# Revit family: 859-002X-001 DN65-300
name_source: partatom
category: Pipe Accessories
units: mm (PartAtom-declared; Revit-internal decimal feet)

## family parameters
Always vertical = Yes
Cut with Voids When Loaded = No
Part Type = Valve - Breaks Into
Round Connector Dimension = Use Diameter
Shared = No
Work Plane-Based = No

## types (42) — shared parameters
10 = 10 mm  [stored 0.0328084 ft]
18 = 11 mm  [stored 0.0360892 ft]
3 = 3 mm  [stored 0.00984252 ft]
50 = 50 mm
8 = 8 mm  [stored 0.0262467 ft]
DN100_PN10/16 Flow range ( 14 - 34) = 859-0100-00-1140021
DN100_PN10/16 Flow range ( 23 - 57) = 859-0100-00-1140022
DN100_PN10/16 Flow range ( 47 - 113) = 859-0100-00-1140023
DN100_PN10/16 Flow range ( 7 - 18) = 859-0100-00-1140020
DN125_PN10/16 Flow range ( 13 - 32) = 859-0125-00-1140020
DN125_PN10/16 Flow range ( 21 - 52) = 859-0125-00-1140021
DN125_PN10/16 Flow range ( 32 - 80) = 859-0125-00-1140022
DN125_PN10/16 Flow range ( 48 - 118) = 859-0125-00-1140023
DN150_PN10/16 Flow range ( 115 - 254) = 859-0150-00-1140023
DN150_PN10/16 Flow range ( 30 - 75) = 859-0150-00-1140020
DN150_PN10/16 Flow range ( 50 - 150) = 859-0150-00-1140021
DN150_PN10/16 Flow range ( 80 - 200) = 859-0150-00-1140022
DN200_PN10 Flow range ( 115 - 290) = 859-0200-00-0140021
DN200_PN10 Flow range ( 150 - 339) = 859-0200-00-0140022
DN200_PN10 Flow range ( 190 - 339) = 859-0200-00-0140023
DN200_PN10 Flow range ( 50 - 130) = 859-0200-00-0140020
DN200_PN16 Flow range ( 115 - 290) = 859-0200-00-1140021
DN200_PN16 Flow range ( 150 - 365) = 859-0200-00-1140022
DN200_PN16 Flow range ( 190 - 452) = 859-0200-00-1140023
DN200_PN16 Flow range ( 50 - 130) = 859-0200-00-1140020
DN250_PN10 Flow range ( 140 - 350) = 859-0250-00-0140021
DN250_PN10 Flow range ( 230 - 530) = 859-0250-00-0140022
DN250_PN10 Flow range ( 280 - 530) = 859-0250-00-0140023
DN250_PN10 Flow range ( 85 - 200) = 859-0250-00-0140020
DN250_PN16 Flow range ( 140 - 350) = 859-0250-00-1140021
DN250_PN16 Flow range ( 230 - 570) = 859-0250-00-1140022
DN250_PN16 Flow range ( 280 - 690) = 859-0250-00-1140023
DN250_PN16 Flow range ( 85 - 200) = 859-0250-00-1140020
DN300_PN10 Flow range ( 120 - 300) = 859-0300-00-0140020
DN300_PN10 Flow range ( 175 - 430) = 859-0300-00-0140021
DN300_PN10 Flow range ( 340 - 762) = 859-0300-00-0140022
DN300_PN10 Flow range ( 460 - 762) = 859-0300-00-0140023
DN300_PN16 Flow range ( 120 - 300) = 859-0300-00-1140020
DN300_PN16 Flow range ( 175 - 430) = 859-0300-00-1140021
DN300_PN16 Flow range ( 340 - 825) = 859-0300-00-1140022
DN300_PN16 Flow range ( 460 - 1017) = 859-0300-00-1140023
DN65_PN10/16 Flow range ( 17 - 42) = 859-0065-00-1140022
DN65_PN10/16 Flow range ( 5 - 15) = 859-0065-00-1140020
DN65_PN10/16 Flow range ( 8 - 20) = 859-0065-00-1140021
DN80_PN10/16 Flow range ( 14 - 36) = 859-0080-00-1140021
DN80_PN10/16 Flow range ( 27 - 65) = 859-0080-00-1140022
DN80_PN10/16 Flow range ( 7 - 18) = 859-0080-00-1140020
Description_ = AVK CONTROL VALVE, CONSTANT FLOW, PN10/16
Orifice_FL_T = 14 mm  [stored 0.0459318 ft]
Search_table = 859-002X-001 DN65-300
URL_product_pages = https://www.avkvalves.com
zero-valued in all types: 0, Default Elevation

## per-type parameters (varying)
- DN065_PN10/16 Flow range ( 5 - 15): Actuator_L=72 mm; Actuator_L1=65 mm; Actuator_d=25 mm  [stored 0.082021 ft]; Body_H=111 mm; Body_Rib_L=46 mm; Bolt_Dia=20 mm  [stored 0.0656168 ft]; Bonnet_D=56 mm; Bonnet_D1=111 mm; Bonnet_R=117 mm; Bonnet_dim1=78 mm; Bonnet_dim1_H=30 mm  [stored 0.0984252 ft]; Bonnet_dim1_H1=188 mm; Bonnet_dim2=39 mm; Bonnet_dim3=29 mm  [stored 0.0951444 ft]; Bore=33 mm; Bore1=39 mm; Bore2=52 mm; Centre_D=25 mm  [stored 0.082021 ft]; Centre_D1=20 mm  [stored 0.0656168 ft]; Centre_nut=19 mm  [stored 0.062336 ft]; Control_dim1=7 mm  [stored 0.0229659 ft]; Control_dim2=35 mm  [stored 0.114829 ft]; Control_dim3=4 mm  [stored 0.0131234 ft]; Control_dim4=100 mm; Control_dim5=10 mm  [stored 0.0328084 ft]; Control_dim6=12 mm  [stored 0.0393701 ft]; Control_dim7=21 mm  [stored 0.0688976 ft]; D=93 mm; DN=65 mm; FL_T=19 mm  [stored 0.062336 ft]; H3=356 mm; H33=60 mm; H4=120 mm; L=290 mm; L3=128 mm; Nut_Dim1=25 mm  [stored 0.082021 ft]; Nut_Dim2=3 mm  [stored 0.00984252 ft]; Nut_T=15 mm  [stored 0.0492126 ft]; Orifice_FL=63 mm; Raised_R=24 mm  [stored 0.0787402 ft]; Raised_dis=3 mm  [stored 0.00984252 ft]; Sweep_R=11 mm  [stored 0.0360892 ft]; Thickness=11 mm  [stored 0.0360892 ft]; Thickness1=14 mm  [stored 0.0459318 ft]; Total_L=305 mm; W=124 mm; W1=131 mm; W11=104 mm; W2=161 mm; W22=129 mm; centre=51 mm; dim1=52 mm; nut_dim=56 mm; sweep=18 mm  [stored 0.0590551 ft]; sweep/2=4 mm  [stored 0.0131234 ft]; sweep1=8 mm  [stored 0.0262467 ft]; sweep_D=15 mm  [stored 0.0492126 ft]; sweep_H=171 mm; sweep_H1=42 mm  [stored 0.137795 ft]; sweep_box1=10 mm  [stored 0.0328084 ft]; sweep_box2=10 mm  [stored 0.0328084 ft]; w1=93 mm; w2=93 mm
- DN065_PN10/16 Flow range ( 8 - 20): Actuator_L=72 mm; Actuator_L1=65 mm; Actuator_d=25 mm  [stored 0.082021 ft]; Body_H=111 mm; Body_Rib_L=46 mm; Bolt_Dia=20 mm  [stored 0.0656168 ft]; Bonnet_D=56 mm; Bonnet_D1=111 mm; Bonnet_R=117 mm; Bonnet_dim1=78 mm; Bonnet_dim1_H=30 mm  [stored 0.0984252 ft]; Bonnet_dim1_H1=188 mm; Bonnet_dim2=39 mm; Bonnet_dim3=29 mm  [stored 0.0951444 ft]; Bore=33 mm; Bore1=39 mm; Bore2=52 mm; Centre_D=25 mm  [stored 0.082021 ft]; Centre_D1=20 mm  [stored 0.0656168 ft]; Centre_nut=19 mm  [stored 0.062336 ft]; Control_dim1=7 mm  [stored 0.0229659 ft]; Control_dim2=35 mm  [stored 0.114829 ft]; Control_dim3=4 mm  [stored 0.0131234 ft]; Control_dim4=100 mm; Control_dim5=10 mm  [stored 0.0328084 ft]; Control_dim6=12 mm  [stored 0.0393701 ft]; Control_dim7=21 mm  [stored 0.0688976 ft]; D=93 mm; DN=65 mm; FL_T=19 mm  [stored 0.062336 ft]; H3=356 mm; H33=60 mm; H4=120 mm; L=290 mm; L3=128 mm; Nut_Dim1=25 mm  [stored 0.082021 ft]; Nut_Dim2=3 mm  [stored 0.00984252 ft]; Nut_T=15 mm  [stored 0.0492126 ft]; Orifice_FL=63 mm; Raised_R=24 mm  [stored 0.0787402 ft]; Raised_dis=3 mm  [stored 0.00984252 ft]; Sweep_R=11 mm  [stored 0.0360892 ft]; Thickness=11 mm  [stored 0.0360892 ft]; Thickness1=14 mm  [stored 0.0459318 ft]; Total_L=305 mm; W=124 mm; W1=131 mm; W11=104 mm; W2=161 mm; W22=129 mm; centre=51 mm; dim1=52 mm; nut_dim=56 mm; sweep=18 mm  [stored 0.0590551 ft]; sweep/2=4 mm  [stored 0.0131234 ft]; sweep1=8 mm  [stored 0.0262467 ft]; sweep_D=15 mm  [stored 0.0492126 ft]; sweep_H=171 mm; sweep_H1=42 mm  [stored 0.137795 ft]; sweep_box1=10 mm  [stored 0.0328084 ft]; sweep_box2=10 mm  [stored 0.0328084 ft]; w1=93 mm; w2=93 mm
- DN065_PN10/16 Flow range ( 17 - 42): Actuator_L=72 mm; Actuator_L1=65 mm; Actuator_d=25 mm  [stored 0.082021 ft]; Body_H=111 mm; Body_Rib_L=46 mm; Bolt_Dia=20 mm  [stored 0.0656168 ft]; Bonnet_D=56 mm; Bonnet_D1=111 mm; Bonnet_R=117 mm; Bonnet_dim1=78 mm; Bonnet_dim1_H=30 mm  [stored 0.0984252 ft]; Bonnet_dim1_H1=188 mm; Bonnet_dim2=39 mm; Bonnet_dim3=29 mm  [stored 0.0951444 ft]; Bore=33 mm; Bore1=39 mm; Bore2=52 mm; Centre_D=25 mm  [stored 0.082021 ft]; Centre_D1=20 mm  [stored 0.0656168 ft]; Centre_nut=19 mm  [stored 0.062336 ft]; Control_dim1=7 mm  [stored 0.0229659 ft]; Control_dim2=35 mm  [stored 0.114829 ft]; Control_dim3=4 mm  [stored 0.0131234 ft]; Control_dim4=100 mm; Control_dim5=10 mm  [stored 0.0328084 ft]; Control_dim6=12 mm  [stored 0.0393701 ft]; Control_dim7=21 mm  [stored 0.0688976 ft]; D=93 mm; DN=65 mm; FL_T=19 mm  [stored 0.062336 ft]; H3=356 mm; H33=60 mm; H4=120 mm; L=290 mm; L3=128 mm; Nut_Dim1=25 mm  [stored 0.082021 ft]; Nut_Dim2=3 mm  [stored 0.00984252 ft]; Nut_T=15 mm  [stored 0.0492126 ft]; Orifice_FL=63 mm; Raised_R=24 mm  [stored 0.0787402 ft]; Raised_dis=3 mm  [stored 0.00984252 ft]; Sweep_R=11 mm  [stored 0.0360892 ft]; Thickness=11 mm  [stored 0.0360892 ft]; Thickness1=14 mm  [stored 0.0459318 ft]; Total_L=305 mm; W=124 mm; W1=131 mm; W11=104 mm; W2=161 mm; W22=129 mm; centre=51 mm; dim1=52 mm; nut_dim=56 mm; sweep=18 mm  [stored 0.0590551 ft]; sweep/2=4 mm  [stored 0.0131234 ft]; sweep1=8 mm  [stored 0.0262467 ft]; sweep_D=15 mm  [stored 0.0492126 ft]; sweep_H=171 mm; sweep_H1=42 mm  [stored 0.137795 ft]; sweep_box1=10 mm  [stored 0.0328084 ft]; sweep_box2=10 mm  [stored 0.0328084 ft]; w1=93 mm; w2=93 mm
- DN080_PN10/16 Flow range ( 7 - 18): Actuator_L=124 mm; Actuator_L1=111 mm; Actuator_d=63 mm; Body_H=276 mm; Body_Rib_L=115 mm; Bolt_Dia=33 mm; Bonnet_D=138 mm; Bonnet_D1=276 mm; Bonnet_R=290 mm; Bonnet_dim1=193 mm; Bonnet_dim1_H=26 mm; Bonnet_dim1_H1=362 mm; Bonnet_dim2=97 mm; Bonnet_dim3=72 mm; Bore=150 mm; Bore1=180 mm; Bore2=240 mm; Centre_D=80 mm; Centre_D1=64 mm; Centre_nut=60 mm; Control_dim1=18 mm  [stored 0.0590551 ft]; Control_dim2=87 mm; Control_dim3=9 mm  [stored 0.0295276 ft]; Control_dim4=248 mm; Control_dim5=24 mm  [stored 0.0787402 ft]; Control_dim6=29 mm  [stored 0.0951444 ft]; Control_dim7=53 mm; D=230 mm; DN=300 mm; FL_T=25 mm  [stored 0.082021 ft]; H3=736 mm; H33=115 mm; H4=231 mm; L=850 mm; L3=319 mm; Nut_Dim1=42 mm  [stored 0.137795 ft]; Nut_Dim2=7 mm  [stored 0.0229659 ft]; Nut_T=20 mm  [stored 0.0656168 ft]; Orifice_FL=189 mm; Raised_R=32 mm  [stored 0.104987 ft]; Raised_dis=4 mm  [stored 0.0131234 ft]; Sweep_R=19 mm  [stored 0.062336 ft]; Thickness=15 mm  [stored 0.0492126 ft]; Thickness1=18 mm  [stored 0.0590551 ft]; Total_L=865 mm; W=263 mm; W1=275 mm; W11=225 mm; W2=275 mm; W22=220 mm; centre=234 mm; dim1=110 mm; nut_dim=138 mm; sweep=30 mm  [stored 0.0984252 ft]; sweep/2=6 mm  [stored 0.019685 ft]; sweep1=13 mm  [stored 0.0426509 ft]; sweep_D=25 mm  [stored 0.082021 ft]; sweep_H=329 mm; sweep_H1=37 mm; sweep_box1=32 mm  [stored 0.104987 ft]; sweep_box2=16 mm  [stored 0.0524934 ft]; w1=275 mm; w2=275 mm
- DN080_PN10/16 Flow range ( 14 - 36): Actuator_L=72 mm; Actuator_L1=65 mm; Actuator_d=28 mm  [stored 0.0918635 ft]; Body_H=120 mm; Body_Rib_L=50 mm; Bolt_Dia=20 mm  [stored 0.0656168 ft]; Bonnet_D=60 mm; Bonnet_D1=120 mm; Bonnet_R=126 mm; Bonnet_dim1=84 mm; Bonnet_dim1_H=29 mm  [stored 0.0951444 ft]; Bonnet_dim1_H1=197 mm; Bonnet_dim2=42 mm  [stored 0.137795 ft]; Bonnet_dim3=32 mm  [stored 0.104987 ft]; Bore=40 mm  [stored 0.131234 ft]; Bore1=48 mm; Bore2=64 mm; Centre_D=25 mm  [stored 0.082021 ft]; Centre_D1=20 mm  [stored 0.0656168 ft]; Centre_nut=19 mm  [stored 0.062336 ft]; Control_dim1=8 mm  [stored 0.0262467 ft]; Control_dim2=38 mm; Control_dim3=4 mm  [stored 0.0131234 ft]; Control_dim4=108 mm; Control_dim5=11 mm  [stored 0.0360892 ft]; Control_dim6=13 mm  [stored 0.0426509 ft]; Control_dim7=23 mm; D=100 mm; DN=80 mm; FL_T=19 mm  [stored 0.062336 ft]; H3=375 mm; H33=63 mm; H4=125 mm; L=310 mm; L3=139 mm; Nut_Dim1=25 mm  [stored 0.082021 ft]; Nut_Dim2=3 mm  [stored 0.00984252 ft]; Nut_T=15 mm  [stored 0.0492126 ft]; Orifice_FL=71 mm; Raised_R=24 mm  [stored 0.0787402 ft]; Raised_dis=3 mm  [stored 0.00984252 ft]; Sweep_R=11 mm  [stored 0.0360892 ft]; Thickness=11 mm  [stored 0.0360892 ft]; Thickness1=14 mm  [stored 0.0459318 ft]; Total_L=325 mm; W=124 mm; W1=131 mm; W11=104 mm; W2=161 mm; W22=129 mm; centre=62 mm; dim1=52 mm; nut_dim=60 mm; sweep=18 mm  [stored 0.0590551 ft]; sweep/2=4 mm  [stored 0.0131234 ft]; sweep1=8 mm  [stored 0.0262467 ft]; sweep_D=15 mm  [stored 0.0492126 ft]; sweep_H=179 mm; sweep_H1=41 mm; sweep_box1=10 mm  [stored 0.0328084 ft]; sweep_box2=10 mm  [stored 0.0328084 ft]; w1=100 mm; w2=100 mm
- DN080_PN10/16 Flow range ( 27 - 65): Actuator_L=72 mm; Actuator_L1=65 mm; Actuator_d=28 mm  [stored 0.0918635 ft]; Body_H=120 mm; Body_Rib_L=50 mm; Bolt_Dia=20 mm  [stored 0.0656168 ft]; Bonnet_D=60 mm; Bonnet_D1=120 mm; Bonnet_R=126 mm; Bonnet_dim1=84 mm; Bonnet_dim1_H=29 mm  [stored 0.0951444 ft]; Bonnet_dim1_H1=197 mm; Bonnet_dim2=42 mm  [stored 0.137795 ft]; Bonnet_dim3=32 mm  [stored 0.104987 ft]; Bore=40 mm  [stored 0.131234 ft]; Bore1=48 mm; Bore2=64 mm; Centre_D=25 mm  [stored 0.082021 ft]; Centre_D1=20 mm  [stored 0.0656168 ft]; Centre_nut=19 mm  [stored 0.062336 ft]; Control_dim1=8 mm  [stored 0.0262467 ft]; Control_dim2=38 mm; Control_dim3=4 mm  [stored 0.0131234 ft]; Control_dim4=108 mm; Control_dim5=11 mm  [stored 0.0360892 ft]; Control_dim6=13 mm  [stored 0.0426509 ft]; Control_dim7=23 mm; D=100 mm; DN=80 mm; FL_T=19 mm  [stored 0.062336 ft]; H3=375 mm; H33=63 mm; H4=125 mm; L=310 mm; L3=139 mm; Nut_Dim1=25 mm  [stored 0.082021 ft]; Nut_Dim2=3 mm  [stored 0.00984252 ft]; Nut_T=15 mm  [stored 0.0492126 ft]; Orifice_FL=71 mm; Raised_R=24 mm  [stored 0.0787402 ft]; Raised_dis=3 mm  [stored 0.00984252 ft]; Sweep_R=11 mm  [stored 0.0360892 ft]; Thickness=11 mm  [stored 0.0360892 ft]; Thickness1=14 mm  [stored 0.0459318 ft]; Total_L=325 mm; W=124 mm; W1=131 mm; W11=104 mm; W2=161 mm; W22=129 mm; centre=63 mm; dim1=52 mm; nut_dim=60 mm; sweep=18 mm  [stored 0.0590551 ft]; sweep/2=4 mm  [stored 0.0131234 ft]; sweep1=8 mm  [stored 0.0262467 ft]; sweep_D=15 mm  [stored 0.0492126 ft]; sweep_H=179 mm; sweep_H1=41 mm; sweep_box1=10 mm  [stored 0.0328084 ft]; sweep_box2=10 mm  [stored 0.0328084 ft]; w1=100 mm; w2=100 mm
- DN100_PN10/16 Flow range ( 7 - 18): Actuator_L=72 mm; Actuator_L1=65 mm; Actuator_d=30 mm  [stored 0.0984252 ft]; Body_H=132 mm; Body_Rib_L=55 mm; Bolt_Dia=20 mm  [stored 0.0656168 ft]; Bonnet_D=66 mm; Bonnet_D1=132 mm; Bonnet_R=139 mm; Bonnet_dim1=92 mm; Bonnet_dim1_H=26 mm; Bonnet_dim1_H1=203 mm; Bonnet_dim2=46 mm; Bonnet_dim3=35 mm  [stored 0.114829 ft]; Bore=50 mm; Bore1=60 mm; Bore2=80 mm; Centre_D=30 mm  [stored 0.0984252 ft]; Centre_D1=24 mm  [stored 0.0787402 ft]; Centre_nut=23 mm; Control_dim1=9 mm  [stored 0.0295276 ft]; Control_dim2=42 mm  [stored 0.137795 ft]; Control_dim3=4 mm  [stored 0.0131234 ft]; Control_dim4=119 mm; Control_dim5=12 mm  [stored 0.0393701 ft]; Control_dim6=14 mm  [stored 0.0459318 ft]; Control_dim7=25 mm  [stored 0.082021 ft]; D=110 mm; DN=100 mm; FL_T=19 mm  [stored 0.062336 ft]; H3=394 mm; H33=65 mm; H4=130 mm; L=350 mm; L3=152 mm; Nut_Dim1=25 mm  [stored 0.082021 ft]; Nut_Dim2=3 mm  [stored 0.00984252 ft]; Nut_T=15 mm  [stored 0.0492126 ft]; Orifice_FL=81 mm; Raised_R=24 mm  [stored 0.0787402 ft]; Raised_dis=3 mm  [stored 0.00984252 ft]; Sweep_R=11 mm  [stored 0.0360892 ft]; Thickness=11 mm  [stored 0.0360892 ft]; Thickness1=14 mm  [stored 0.0459318 ft]; Total_L=365 mm; W=124 mm; W1=131 mm; W11=104 mm; W2=161 mm; W22=129 mm; centre=78 mm; dim1=52 mm; nut_dim=66 mm; sweep=18 mm  [stored 0.0590551 ft]; sweep/2=4 mm  [stored 0.0131234 ft]; sweep1=8 mm  [stored 0.0262467 ft]; sweep_D=15 mm  [stored 0.0492126 ft]; sweep_H=185 mm; sweep_H1=37 mm; sweep_box1=12 mm  [stored 0.0393701 ft]; sweep_box2=10 mm  [stored 0.0328084 ft]; w1=110 mm; w2=110 mm
- DN100_PN10/16 Flow range ( 14 - 34): Actuator_L=72 mm; Actuator_L1=65 mm; Actuator_d=30 mm  [stored 0.0984252 ft]; Body_H=132 mm; Body_Rib_L=55 mm; Bolt_Dia=20 mm  [stored 0.0656168 ft]; Bonnet_D=66 mm; Bonnet_D1=132 mm; Bonnet_R=139 mm; Bonnet_dim1=92 mm; Bonnet_dim1_H=26 mm; Bonnet_dim1_H1=203 mm; Bonnet_dim2=46 mm; Bonnet_dim3=35 mm  [stored 0.114829 ft]; Bore=50 mm; Bore1=60 mm; Bore2=80 mm; Centre_D=30 mm  [stored 0.0984252 ft]; Centre_D1=24 mm  [stored 0.0787402 ft]; Centre_nut=23 mm; Control_dim1=9 mm  [stored 0.0295276 ft]; Control_dim2=42 mm  [stored 0.137795 ft]; Control_dim3=4 mm  [stored 0.0131234 ft]; Control_dim4=119 mm; Control_dim5=12 mm  [stored 0.0393701 ft]; Control_dim6=14 mm  [stored 0.0459318 ft]; Control_dim7=25 mm  [stored 0.082021 ft]; D=110 mm; DN=100 mm; FL_T=19 mm  [stored 0.062336 ft]; H3=394 mm; H33=65 mm; H4=130 mm; L=350 mm; L3=152 mm; Nut_Dim1=25 mm  [stored 0.082021 ft]; Nut_Dim2=3 mm  [stored 0.00984252 ft]; Nut_T=15 mm  [stored 0.0492126 ft]; Orifice_FL=81 mm; Raised_R=24 mm  [stored 0.0787402 ft]; Raised_dis=3 mm  [stored 0.00984252 ft]; Sweep_R=11 mm  [stored 0.0360892 ft]; Thickness=11 mm  [stored 0.0360892 ft]; Thickness1=14 mm  [stored 0.0459318 ft]; Total_L=365 mm; W=124 mm; W1=131 mm; W11=104 mm; W2=161 mm; W22=129 mm; centre=78 mm; dim1=52 mm; nut_dim=66 mm; sweep=18 mm  [stored 0.0590551 ft]; sweep/2=4 mm  [stored 0.0131234 ft]; sweep1=8 mm  [stored 0.0262467 ft]; sweep_D=15 mm  [stored 0.0492126 ft]; sweep_H=185 mm; sweep_H1=37 mm; sweep_box1=12 mm  [stored 0.0393701 ft]; sweep_box2=10 mm  [stored 0.0328084 ft]; w1=110 mm; w2=110 mm
- DN100_PN10/16 Flow range ( 23 - 57): Actuator_L=72 mm; Actuator_L1=65 mm; Actuator_d=30 mm  [stored 0.0984252 ft]; Body_H=132 mm; Body_Rib_L=55 mm; Bolt_Dia=20 mm  [stored 0.0656168 ft]; Bonnet_D=66 mm; Bonnet_D1=132 mm; Bonnet_R=139 mm; Bonnet_dim1=92 mm; Bonnet_dim1_H=26 mm; Bonnet_dim1_H1=203 mm; Bonnet_dim2=46 mm; Bonnet_dim3=35 mm  [stored 0.114829 ft]; Bore=50 mm; Bore1=60 mm; Bore2=80 mm; Centre_D=30 mm  [stored 0.0984252 ft]; Centre_D1=24 mm  [stored 0.0787402 ft]; Centre_nut=23 mm; Control_dim1=9 mm  [stored 0.0295276 ft]; Control_dim2=42 mm  [stored 0.137795 ft]; Control_dim3=4 mm  [stored 0.0131234 ft]; Control_dim4=119 mm; Control_dim5=12 mm  [stored 0.0393701 ft]; Control_dim6=14 mm  [stored 0.0459318 ft]; Control_dim7=25 mm  [stored 0.082021 ft]; D=110 mm; DN=100 mm; FL_T=19 mm  [stored 0.062336 ft]; H3=394 mm; H33=65 mm; H4=130 mm; L=350 mm; L3=152 mm; Nut_Dim1=25 mm  [stored 0.082021 ft]; Nut_Dim2=3 mm  [stored 0.00984252 ft]; Nut_T=15 mm  [stored 0.0492126 ft]; Orifice_FL=81 mm; Raised_R=24 mm  [stored 0.0787402 ft]; Raised_dis=3 mm  [stored 0.00984252 ft]; Sweep_R=11 mm  [stored 0.0360892 ft]; Thickness=11 mm  [stored 0.0360892 ft]; Thickness1=14 mm  [stored 0.0459318 ft]; Total_L=365 mm; W=124 mm; W1=131 mm; W11=104 mm; W2=161 mm; W22=129 mm; centre=78 mm; dim1=52 mm; nut_dim=66 mm; sweep=18 mm  [stored 0.0590551 ft]; sweep/2=4 mm  [stored 0.0131234 ft]; sweep1=8 mm  [stored 0.0262467 ft]; sweep_D=15 mm  [stored 0.0492126 ft]; sweep_H=185 mm; sweep_H1=37 mm; sweep_box1=12 mm  [stored 0.0393701 ft]; sweep_box2=10 mm  [stored 0.0328084 ft]; w1=110 mm; w2=110 mm
- DN100_PN10/16 Flow range ( 47 - 113): Actuator_L=72 mm; Actuator_L1=65 mm; Actuator_d=30 mm  [stored 0.0984252 ft]; Body_H=132 mm; Body_Rib_L=55 mm; Bolt_Dia=20 mm  [stored 0.0656168 ft]; Bonnet_D=66 mm; Bonnet_D1=132 mm; Bonnet_R=139 mm; Bonnet_dim1=92 mm; Bonnet_dim1_H=26 mm; Bonnet_dim1_H1=203 mm; Bonnet_dim2=46 mm; Bonnet_dim3=35 mm  [stored 0.114829 ft]; Bore=50 mm; Bore1=60 mm; Bore2=80 mm; Centre_D=30 mm  [stored 0.0984252 ft]; Centre_D1=24 mm  [stored 0.0787402 ft]; Centre_nut=23 mm; Control_dim1=9 mm  [stored 0.0295276 ft]; Control_dim2=42 mm  [stored 0.137795 ft]; Control_dim3=4 mm  [stored 0.0131234 ft]; Control_dim4=119 mm; Control_dim5=12 mm  [stored 0.0393701 ft]; Control_dim6=14 mm  [stored 0.0459318 ft]; Control_dim7=25 mm  [stored 0.082021 ft]; D=110 mm; DN=100 mm; FL_T=19 mm  [stored 0.062336 ft]; H3=394 mm; H33=65 mm; H4=130 mm; L=350 mm; L3=152 mm; Nut_Dim1=25 mm  [stored 0.082021 ft]; Nut_Dim2=3 mm  [stored 0.00984252 ft]; Nut_T=15 mm  [stored 0.0492126 ft]; Orifice_FL=81 mm; Raised_R=24 mm  [stored 0.0787402 ft]; Raised_dis=3 mm  [stored 0.00984252 ft]; Sweep_R=11 mm  [stored 0.0360892 ft]; Thickness=11 mm  [stored 0.0360892 ft]; Thickness1=14 mm  [stored 0.0459318 ft]; Total_L=365 mm; W=124 mm; W1=131 mm; W11=104 mm; W2=161 mm; W22=129 mm; centre=78 mm; dim1=52 mm; nut_dim=66 mm; sweep=18 mm  [stored 0.0590551 ft]; sweep/2=4 mm  [stored 0.0131234 ft]; sweep1=8 mm  [stored 0.0262467 ft]; sweep_D=15 mm  [stored 0.0492126 ft]; sweep_H=185 mm; sweep_H1=37 mm; sweep_box1=12 mm  [stored 0.0393701 ft]; sweep_box2=10 mm  [stored 0.0328084 ft]; w1=110 mm; w2=110 mm
- DN125_PN10/16 Flow range ( 13 - 32): Actuator_L=72 mm; Actuator_L1=65 mm; Actuator_d=34 mm; Body_H=150 mm; Body_Rib_L=63 mm; Bolt_Dia=20 mm  [stored 0.0656168 ft]; Bonnet_D=75 mm; Bonnet_D1=150 mm; Bonnet_R=158 mm; Bonnet_dim1=105 mm; Bonnet_dim1_H=19 mm  [stored 0.062336 ft]; Bonnet_dim1_H1=206 mm; Bonnet_dim2=53 mm; Bonnet_dim3=39 mm; Bore=63 mm; Bore1=75 mm; Bore2=100 mm; Centre_D=40 mm  [stored 0.131234 ft]; Centre_D1=32 mm  [stored 0.104987 ft]; Centre_nut=30 mm  [stored 0.0984252 ft]; Control_dim1=10 mm  [stored 0.0328084 ft]; Control_dim2=47 mm; Control_dim3=5 mm  [stored 0.0164042 ft]; Control_dim4=135 mm; Control_dim5=13 mm  [stored 0.0426509 ft]; Control_dim6=16 mm  [stored 0.0524934 ft]; Control_dim7=29 mm  [stored 0.0951444 ft]; D=125 mm; DN=125 mm; FL_T=19 mm  [stored 0.062336 ft]; H3=413 mm; H33=66 mm; H4=131 mm; L=400 mm; L3=173 mm; Nut_Dim1=25 mm  [stored 0.082021 ft]; Nut_Dim2=4 mm  [stored 0.0131234 ft]; Nut_T=15 mm  [stored 0.0492126 ft]; Orifice_FL=96 mm; Raised_R=25 mm  [stored 0.082021 ft]; Raised_dis=3 mm  [stored 0.00984252 ft]; Sweep_R=11 mm  [stored 0.0360892 ft]; Thickness=11 mm  [stored 0.0360892 ft]; Thickness1=14 mm  [stored 0.0459318 ft]; Total_L=415 mm; W=124 mm; W1=131 mm; W11=104 mm; W2=161 mm; W22=129 mm; centre=98 mm; dim1=52 mm; nut_dim=75 mm; sweep=18 mm  [stored 0.0590551 ft]; sweep/2=4 mm  [stored 0.0131234 ft]; sweep1=8 mm  [stored 0.0262467 ft]; sweep_D=15 mm  [stored 0.0492126 ft]; sweep_H=187 mm; sweep_H1=26 mm; sweep_box1=16 mm  [stored 0.0524934 ft]; sweep_box2=10 mm  [stored 0.0328084 ft]; w1=125 mm; w2=125 mm
- DN125_PN10/16 Flow range ( 21 - 52): Actuator_L=72 mm; Actuator_L1=65 mm; Actuator_d=34 mm; Body_H=150 mm; Body_Rib_L=63 mm; Bolt_Dia=20 mm  [stored 0.0656168 ft]; Bonnet_D=75 mm; Bonnet_D1=150 mm; Bonnet_R=158 mm; Bonnet_dim1=105 mm; Bonnet_dim1_H=19 mm  [stored 0.062336 ft]; Bonnet_dim1_H1=206 mm; Bonnet_dim2=53 mm; Bonnet_dim3=39 mm; Bore=63 mm; Bore1=75 mm; Bore2=100 mm; Centre_D=40 mm  [stored 0.131234 ft]; Centre_D1=32 mm  [stored 0.104987 ft]; Centre_nut=30 mm  [stored 0.0984252 ft]; Control_dim1=10 mm  [stored 0.0328084 ft]; Control_dim2=47 mm; Control_dim3=5 mm  [stored 0.0164042 ft]; Control_dim4=135 mm; Control_dim5=13 mm  [stored 0.0426509 ft]; Control_dim6=16 mm  [stored 0.0524934 ft]; Control_dim7=29 mm  [stored 0.0951444 ft]; D=125 mm; DN=125 mm; FL_T=19 mm  [stored 0.062336 ft]; H3=413 mm; H33=66 mm; H4=131 mm; L=400 mm; L3=173 mm; Nut_Dim1=25 mm  [stored 0.082021 ft]; Nut_Dim2=4 mm  [stored 0.0131234 ft]; Nut_T=15 mm  [stored 0.0492126 ft]; Orifice_FL=96 mm; Raised_R=25 mm  [stored 0.082021 ft]; Raised_dis=3 mm  [stored 0.00984252 ft]; Sweep_R=11 mm  [stored 0.0360892 ft]; Thickness=11 mm  [stored 0.0360892 ft]; Thickness1=14 mm  [stored 0.0459318 ft]; Total_L=415 mm; W=124 mm; W1=131 mm; W11=104 mm; W2=161 mm; W22=129 mm; centre=98 mm; dim1=52 mm; nut_dim=75 mm; sweep=18 mm  [stored 0.0590551 ft]; sweep/2=4 mm  [stored 0.0131234 ft]; sweep1=8 mm  [stored 0.0262467 ft]; sweep_D=15 mm  [stored 0.0492126 ft]; sweep_H=187 mm; sweep_H1=26 mm; sweep_box1=16 mm  [stored 0.0524934 ft]; sweep_box2=10 mm  [stored 0.0328084 ft]; w1=125 mm; w2=125 mm
- DN125_PN10/16 Flow range ( 32 - 80): Actuator_L=72 mm; Actuator_L1=65 mm; Actuator_d=34 mm; Body_H=150 mm; Body_Rib_L=63 mm; Bolt_Dia=20 mm  [stored 0.0656168 ft]; Bonnet_D=75 mm; Bonnet_D1=150 mm; Bonnet_R=158 mm; Bonnet_dim1=105 mm; Bonnet_dim1_H=19 mm  [stored 0.062336 ft]; Bonnet_dim1_H1=206 mm; Bonnet_dim2=53 mm; Bonnet_dim3=39 mm; Bore=63 mm; Bore1=75 mm; Bore2=100 mm; Centre_D=40 mm  [stored 0.131234 ft]; Centre_D1=32 mm  [stored 0.104987 ft]; Centre_nut=30 mm  [stored 0.0984252 ft]; Control_dim1=10 mm  [stored 0.0328084 ft]; Control_dim2=47 mm; Control_dim3=5 mm  [stored 0.0164042 ft]; Control_dim4=135 mm; Control_dim5=13 mm  [stored 0.0426509 ft]; Control_dim6=16 mm  [stored 0.0524934 ft]; Control_dim7=29 mm  [stored 0.0951444 ft]; D=125 mm; DN=125 mm; FL_T=19 mm  [stored 0.062336 ft]; H3=413 mm; H33=66 mm; H4=131 mm; L=400 mm; L3=173 mm; Nut_Dim1=25 mm  [stored 0.082021 ft]; Nut_Dim2=4 mm  [stored 0.0131234 ft]; Nut_T=15 mm  [stored 0.0492126 ft]; Orifice_FL=96 mm; Raised_R=25 mm  [stored 0.082021 ft]; Raised_dis=3 mm  [stored 0.00984252 ft]; Sweep_R=11 mm  [stored 0.0360892 ft]; Thickness=11 mm  [stored 0.0360892 ft]; Thickness1=14 mm  [stored 0.0459318 ft]; Total_L=415 mm; W=124 mm; W1=131 mm; W11=104 mm; W2=161 mm; W22=129 mm; centre=98 mm; dim1=52 mm; nut_dim=75 mm; sweep=18 mm  [stored 0.0590551 ft]; sweep/2=4 mm  [stored 0.0131234 ft]; sweep1=8 mm  [stored 0.0262467 ft]; sweep_D=15 mm  [stored 0.0492126 ft]; sweep_H=187 mm; sweep_H1=26 mm; sweep_box1=16 mm  [stored 0.0524934 ft]; sweep_box2=10 mm  [stored 0.0328084 ft]; w1=125 mm; w2=125 mm
- DN125_PN10/16 Flow range ( 48 - 118): Actuator_L=72 mm; Actuator_L1=65 mm; Actuator_d=34 mm; Body_H=150 mm; Body_Rib_L=63 mm; Bolt_Dia=20 mm  [stored 0.0656168 ft]; Bonnet_D=75 mm; Bonnet_D1=150 mm; Bonnet_R=158 mm; Bonnet_dim1=105 mm; Bonnet_dim1_H=19 mm  [stored 0.062336 ft]; Bonnet_dim1_H1=206 mm; Bonnet_dim2=53 mm; Bonnet_dim3=39 mm; Bore=63 mm; Bore1=75 mm; Bore2=100 mm; Centre_D=40 mm  [stored 0.131234 ft]; Centre_D1=32 mm  [stored 0.104987 ft]; Centre_nut=30 mm  [stored 0.0984252 ft]; Control_dim1=10 mm  [stored 0.0328084 ft]; Control_dim2=47 mm; Control_dim3=5 mm  [stored 0.0164042 ft]; Control_dim4=135 mm; Control_dim5=13 mm  [stored 0.0426509 ft]; Control_dim6=16 mm  [stored 0.0524934 ft]; Control_dim7=29 mm  [stored 0.0951444 ft]; D=125 mm; DN=125 mm; FL_T=19 mm  [stored 0.062336 ft]; H3=413 mm; H33=66 mm; H4=131 mm; L=400 mm; L3=173 mm; Nut_Dim1=25 mm  [stored 0.082021 ft]; Nut_Dim2=4 mm  [stored 0.0131234 ft]; Nut_T=15 mm  [stored 0.0492126 ft]; Orifice_FL=96 mm; Raised_R=25 mm  [stored 0.082021 ft]; Raised_dis=3 mm  [stored 0.00984252 ft]; Sweep_R=11 mm  [stored 0.0360892 ft]; Thickness=11 mm  [stored 0.0360892 ft]; Thickness1=14 mm  [stored 0.0459318 ft]; Total_L=415 mm; W=124 mm; W1=131 mm; W11=104 mm; W2=161 mm; W22=129 mm; centre=98 mm; dim1=52 mm; nut_dim=75 mm; sweep=18 mm  [stored 0.0590551 ft]; sweep/2=4 mm  [stored 0.0131234 ft]; sweep1=8 mm  [stored 0.0262467 ft]; sweep_D=15 mm  [stored 0.0492126 ft]; sweep_H=187 mm; sweep_H1=26 mm; sweep_box1=16 mm  [stored 0.0524934 ft]; sweep_box2=10 mm  [stored 0.0328084 ft]; w1=125 mm; w2=125 mm
- DN150_PN10/16 Flow range ( 30 - 75): Actuator_L=72 mm; Actuator_L1=65 mm; Actuator_d=39 mm; Body_H=171 mm; Body_Rib_L=71 mm; Bolt_Dia=20 mm  [stored 0.0656168 ft]; Bonnet_D=86 mm; Bonnet_D1=171 mm; Bonnet_R=180 mm; Bonnet_dim1=120 mm; Bonnet_dim1_H=15 mm  [stored 0.0492126 ft]; Bonnet_dim1_H1=221 mm; Bonnet_dim2=60 mm; Bonnet_dim3=45 mm  [stored 0.147638 ft]; Bore=75 mm; Bore1=90 mm; Bore2=120 mm; Centre_D=50 mm; Centre_D1=40 mm  [stored 0.131234 ft]; Centre_nut=38 mm; Control_dim1=11 mm  [stored 0.0360892 ft]; Control_dim2=54 mm; Control_dim3=6 mm  [stored 0.019685 ft]; Control_dim4=154 mm; Control_dim5=15 mm  [stored 0.0492126 ft]; Control_dim6=18 mm  [stored 0.0590551 ft]; Control_dim7=33 mm; D=143 mm; DN=150 mm; FL_T=19 mm  [stored 0.062336 ft]; H3=451 mm; H33=70 mm; H4=141 mm; L=480 mm; L3=198 mm; Nut_Dim1=25 mm  [stored 0.082021 ft]; Nut_Dim2=4 mm  [stored 0.0131234 ft]; Nut_T=15 mm  [stored 0.0492126 ft]; Orifice_FL=109 mm; Raised_R=27 mm; Raised_dis=3 mm  [stored 0.00984252 ft]; Sweep_R=11 mm  [stored 0.0360892 ft]; Thickness=11 mm  [stored 0.0360892 ft]; Thickness1=14 mm  [stored 0.0459318 ft]; Total_L=495 mm; W=132 mm; W1=139 mm; W11=112 mm; W2=161 mm; W22=129 mm; centre=117 mm; dim1=56 mm; nut_dim=86 mm; sweep=18 mm  [stored 0.0590551 ft]; sweep/2=4 mm  [stored 0.0131234 ft]; sweep1=8 mm  [stored 0.0262467 ft]; sweep_D=15 mm  [stored 0.0492126 ft]; sweep_H=201 mm; sweep_H1=21 mm  [stored 0.0688976 ft]; sweep_box1=20 mm  [stored 0.0656168 ft]; sweep_box2=10 mm  [stored 0.0328084 ft]; w1=139 mm; w2=161 mm
- DN150_PN10/16 Flow range ( 50 - 150): Actuator_L=72 mm; Actuator_L1=65 mm; Actuator_d=39 mm; Body_H=171 mm; Body_Rib_L=71 mm; Bolt_Dia=20 mm  [stored 0.0656168 ft]; Bonnet_D=86 mm; Bonnet_D1=171 mm; Bonnet_R=180 mm; Bonnet_dim1=120 mm; Bonnet_dim1_H=15 mm  [stored 0.0492126 ft]; Bonnet_dim1_H1=221 mm; Bonnet_dim2=60 mm; Bonnet_dim3=45 mm  [stored 0.147638 ft]; Bore=75 mm; Bore1=90 mm; Bore2=120 mm; Centre_D=50 mm; Centre_D1=40 mm  [stored 0.131234 ft]; Centre_nut=38 mm; Control_dim1=11 mm  [stored 0.0360892 ft]; Control_dim2=54 mm; Control_dim3=6 mm  [stored 0.019685 ft]; Control_dim4=154 mm; Control_dim5=15 mm  [stored 0.0492126 ft]; Control_dim6=18 mm  [stored 0.0590551 ft]; Control_dim7=33 mm; D=143 mm; DN=150 mm; FL_T=19 mm  [stored 0.062336 ft]; H3=451 mm; H33=70 mm; H4=141 mm; L=480 mm; L3=198 mm; Nut_Dim1=25 mm  [stored 0.082021 ft]; Nut_Dim2=4 mm  [stored 0.0131234 ft]; Nut_T=15 mm  [stored 0.0492126 ft]; Orifice_FL=109 mm; Raised_R=27 mm; Raised_dis=3 mm  [stored 0.00984252 ft]; Sweep_R=11 mm  [stored 0.0360892 ft]; Thickness=11 mm  [stored 0.0360892 ft]; Thickness1=14 mm  [stored 0.0459318 ft]; Total_L=495 mm; W=132 mm; W1=139 mm; W11=112 mm; W2=161 mm; W22=129 mm; centre=117 mm; dim1=56 mm; nut_dim=86 mm; sweep=18 mm  [stored 0.0590551 ft]; sweep/2=4 mm  [stored 0.0131234 ft]; sweep1=8 mm  [stored 0.0262467 ft]; sweep_D=15 mm  [stored 0.0492126 ft]; sweep_H=201 mm; sweep_H1=21 mm  [stored 0.0688976 ft]; sweep_box1=20 mm  [stored 0.0656168 ft]; sweep_box2=10 mm  [stored 0.0328084 ft]; w1=139 mm; w2=161 mm
- DN150_PN10/16 Flow range ( 80 - 200): Actuator_L=72 mm; Actuator_L1=65 mm; Actuator_d=39 mm; Body_H=171 mm; Body_Rib_L=71 mm; Bolt_Dia=20 mm  [stored 0.0656168 ft]; Bonnet_D=86 mm; Bonnet_D1=171 mm; Bonnet_R=180 mm; Bonnet_dim1=120 mm; Bonnet_dim1_H=15 mm  [stored 0.0492126 ft]; Bonnet_dim1_H1=221 mm; Bonnet_dim2=60 mm; Bonnet_dim3=45 mm  [stored 0.147638 ft]; Bore=75 mm; Bore1=90 mm; Bore2=120 mm; Centre_D=50 mm; Centre_D1=40 mm  [stored 0.131234 ft]; Centre_nut=38 mm; Control_dim1=11 mm  [stored 0.0360892 ft]; Control_dim2=54 mm; Control_dim3=6 mm  [stored 0.019685 ft]; Control_dim4=154 mm; Control_dim5=15 mm  [stored 0.0492126 ft]; Control_dim6=18 mm  [stored 0.0590551 ft]; Control_dim7=33 mm; D=143 mm; DN=150 mm; FL_T=19 mm  [stored 0.062336 ft]; H3=451 mm; H33=70 mm; H4=141 mm; L=480 mm; L3=198 mm; Nut_Dim1=25 mm  [stored 0.082021 ft]; Nut_Dim2=4 mm  [stored 0.0131234 ft]; Nut_T=15 mm  [stored 0.0492126 ft]; Orifice_FL=109 mm; Raised_R=27 mm; Raised_dis=3 mm  [stored 0.00984252 ft]; Sweep_R=11 mm  [stored 0.0360892 ft]; Thickness=11 mm  [stored 0.0360892 ft]; Thickness1=14 mm  [stored 0.0459318 ft]; Total_L=495 mm; W=132 mm; W1=139 mm; W11=112 mm; W2=161 mm; W22=129 mm; centre=117 mm; dim1=56 mm; nut_dim=86 mm; sweep=18 mm  [stored 0.0590551 ft]; sweep/2=4 mm  [stored 0.0131234 ft]; sweep1=8 mm  [stored 0.0262467 ft]; sweep_D=15 mm  [stored 0.0492126 ft]; sweep_H=201 mm; sweep_H1=21 mm  [stored 0.0688976 ft]; sweep_box1=20 mm  [stored 0.0656168 ft]; sweep_box2=10 mm  [stored 0.0328084 ft]; w1=139 mm; w2=161 mm
- DN150_PN10/16 Flow range ( 115 - 254): Actuator_L=72 mm; Actuator_L1=65 mm; Actuator_d=39 mm; Body_H=171 mm; Body_Rib_L=71 mm; Bolt_Dia=20 mm  [stored 0.0656168 ft]; Bonnet_D=86 mm; Bonnet_D1=171 mm; Bonnet_R=180 mm; Bonnet_dim1=120 mm; Bonnet_dim1_H=15 mm  [stored 0.0492126 ft]; Bonnet_dim1_H1=221 mm; Bonnet_dim2=60 mm; Bonnet_dim3=45 mm  [stored 0.147638 ft]; Bore=75 mm; Bore1=90 mm; Bore2=120 mm; Centre_D=50 mm; Centre_D1=40 mm  [stored 0.131234 ft]; Centre_nut=38 mm; Control_dim1=11 mm  [stored 0.0360892 ft]; Control_dim2=54 mm; Control_dim3=6 mm  [stored 0.019685 ft]; Control_dim4=154 mm; Control_dim5=15 mm  [stored 0.0492126 ft]; Control_dim6=18 mm  [stored 0.0590551 ft]; Control_dim7=33 mm; D=143 mm; DN=150 mm; FL_T=19 mm  [stored 0.062336 ft]; H3=451 mm; H33=70 mm; H4=141 mm; L=480 mm; L3=198 mm; Nut_Dim1=25 mm  [stored 0.082021 ft]; Nut_Dim2=4 mm  [stored 0.0131234 ft]; Nut_T=15 mm  [stored 0.0492126 ft]; Orifice_FL=109 mm; Raised_R=27 mm; Raised_dis=3 mm  [stored 0.00984252 ft]; Sweep_R=11 mm  [stored 0.0360892 ft]; Thickness=11 mm  [stored 0.0360892 ft]; Thickness1=14 mm  [stored 0.0459318 ft]; Total_L=495 mm; W=132 mm; W1=139 mm; W11=112 mm; W2=161 mm; W22=129 mm; centre=117 mm; dim1=56 mm; nut_dim=86 mm; sweep=18 mm  [stored 0.0590551 ft]; sweep/2=4 mm  [stored 0.0131234 ft]; sweep1=8 mm  [stored 0.0262467 ft]; sweep_D=15 mm  [stored 0.0492126 ft]; sweep_H=201 mm; sweep_H1=21 mm  [stored 0.0688976 ft]; sweep_box1=20 mm  [stored 0.0656168 ft]; sweep_box2=10 mm  [stored 0.0328084 ft]; w1=139 mm; w2=161 mm
- DN200_PN10 Flow range ( 50 - 130): Actuator_L=91 mm; Actuator_L1=82 mm; Actuator_d=47 mm; Body_H=204 mm; Body_Rib_L=85 mm; Bolt_Dia=23 mm; Bonnet_D=102 mm; Bonnet_D1=204 mm; Bonnet_R=214 mm; Bonnet_dim1=143 mm; Bonnet_dim1_H=19 mm  [stored 0.062336 ft]; Bonnet_dim1_H1=266 mm; Bonnet_dim2=71 mm; Bonnet_dim3=54 mm; Bore=100 mm; Bore1=120 mm; Bore2=160 mm; Centre_D=60 mm; Centre_D1=48 mm; Centre_nut=45 mm  [stored 0.147638 ft]; Control_dim1=13 mm  [stored 0.0426509 ft]; Control_dim2=64 mm; Control_dim3=7 mm  [stored 0.0229659 ft]; Control_dim4=184 mm; Control_dim5=18 mm  [stored 0.0590551 ft]; Control_dim6=22 mm  [stored 0.0721785 ft]; Control_dim7=39 mm; D=170 mm; DN=200 mm; FL_T=20 mm  [stored 0.0656168 ft]; H3=542 mm; H33=85 mm; H4=170 mm; L=600 mm; L3=236 mm; Nut_Dim1=30 mm  [stored 0.0984252 ft]; Nut_Dim2=5 mm  [stored 0.0164042 ft]; Nut_T=16 mm  [stored 0.0524934 ft]; Orifice_FL=136 mm; Raised_R=28 mm  [stored 0.0918635 ft]; Raised_dis=3 mm  [stored 0.00984252 ft]; Sweep_R=13 mm  [stored 0.0426509 ft]; Thickness=12 mm  [stored 0.0393701 ft]; Thickness1=14 mm  [stored 0.0459318 ft]; Total_L=615 mm; W=193 mm; W1=202 mm; W11=166 mm; W2=202 mm; W22=162 mm; centre=156 mm; dim1=81 mm; nut_dim=102 mm; sweep=21 mm  [stored 0.0688976 ft]; sweep/2=4 mm  [stored 0.0131234 ft]; sweep1=9 mm  [stored 0.0295276 ft]; sweep_D=18 mm  [stored 0.0590551 ft]; sweep_H=242 mm; sweep_H1=26 mm; sweep_box1=24 mm  [stored 0.0787402 ft]; sweep_box2=11 mm  [stored 0.0360892 ft]; w1=202 mm; w2=202 mm
- DN200_PN10 Flow range ( 115 - 290): Actuator_L=91 mm; Actuator_L1=82 mm; Actuator_d=47 mm; Body_H=204 mm; Body_Rib_L=85 mm; Bolt_Dia=23 mm; Bonnet_D=102 mm; Bonnet_D1=204 mm; Bonnet_R=214 mm; Bonnet_dim1=143 mm; Bonnet_dim1_H=19 mm  [stored 0.062336 ft]; Bonnet_dim1_H1=266 mm; Bonnet_dim2=71 mm; Bonnet_dim3=54 mm; Bore=100 mm; Bore1=120 mm; Bore2=160 mm; Centre_D=60 mm; Centre_D1=48 mm; Centre_nut=45 mm  [stored 0.147638 ft]; Control_dim1=13 mm  [stored 0.0426509 ft]; Control_dim2=64 mm; Control_dim3=7 mm  [stored 0.0229659 ft]; Control_dim4=184 mm; Control_dim5=18 mm  [stored 0.0590551 ft]; Control_dim6=22 mm  [stored 0.0721785 ft]; Control_dim7=39 mm; D=170 mm; DN=200 mm; FL_T=20 mm  [stored 0.0656168 ft]; H3=542 mm; H33=85 mm; H4=170 mm; L=600 mm; L3=236 mm; Nut_Dim1=30 mm  [stored 0.0984252 ft]; Nut_Dim2=5 mm  [stored 0.0164042 ft]; Nut_T=16 mm  [stored 0.0524934 ft]; Orifice_FL=136 mm; Raised_R=28 mm  [stored 0.0918635 ft]; Raised_dis=3 mm  [stored 0.00984252 ft]; Sweep_R=13 mm  [stored 0.0426509 ft]; Thickness=12 mm  [stored 0.0393701 ft]; Thickness1=14 mm  [stored 0.0459318 ft]; Total_L=615 mm; W=193 mm; W1=202 mm; W11=166 mm; W2=202 mm; W22=162 mm; centre=156 mm; dim1=81 mm; nut_dim=102 mm; sweep=21 mm  [stored 0.0688976 ft]; sweep/2=4 mm  [stored 0.0131234 ft]; sweep1=9 mm  [stored 0.0295276 ft]; sweep_D=18 mm  [stored 0.0590551 ft]; sweep_H=242 mm; sweep_H1=26 mm; sweep_box1=24 mm  [stored 0.0787402 ft]; sweep_box2=11 mm  [stored 0.0360892 ft]; w1=202 mm; w2=202 mm
- DN200_PN10 Flow range ( 150 - 339): Actuator_L=91 mm; Actuator_L1=82 mm; Actuator_d=47 mm; Body_H=204 mm; Body_Rib_L=85 mm; Bolt_Dia=23 mm; Bonnet_D=102 mm; Bonnet_D1=204 mm; Bonnet_R=214 mm; Bonnet_dim1=143 mm; Bonnet_dim1_H=19 mm  [stored 0.062336 ft]; Bonnet_dim1_H1=266 mm; Bonnet_dim2=71 mm; Bonnet_dim3=54 mm; Bore=100 mm; Bore1=120 mm; Bore2=160 mm; Centre_D=60 mm; Centre_D1=48 mm; Centre_nut=45 mm  [stored 0.147638 ft]; Control_dim1=13 mm  [stored 0.0426509 ft]; Control_dim2=64 mm; Control_dim3=7 mm  [stored 0.0229659 ft]; Control_dim4=184 mm; Control_dim5=18 mm  [stored 0.0590551 ft]; Control_dim6=22 mm  [stored 0.0721785 ft]; Control_dim7=39 mm; D=170 mm; DN=200 mm; FL_T=20 mm  [stored 0.0656168 ft]; H3=542 mm; H33=85 mm; H4=170 mm; L=600 mm; L3=236 mm; Nut_Dim1=30 mm  [stored 0.0984252 ft]; Nut_Dim2=5 mm  [stored 0.0164042 ft]; Nut_T=16 mm  [stored 0.0524934 ft]; Orifice_FL=136 mm; Raised_R=28 mm  [stored 0.0918635 ft]; Raised_dis=3 mm  [stored 0.00984252 ft]; Sweep_R=13 mm  [stored 0.0426509 ft]; Thickness=12 mm  [stored 0.0393701 ft]; Thickness1=14 mm  [stored 0.0459318 ft]; Total_L=615 mm; W=193 mm; W1=202 mm; W11=166 mm; W2=202 mm; W22=162 mm; centre=156 mm; dim1=81 mm; nut_dim=102 mm; sweep=21 mm  [stored 0.0688976 ft]; sweep/2=4 mm  [stored 0.0131234 ft]; sweep1=9 mm  [stored 0.0295276 ft]; sweep_D=18 mm  [stored 0.0590551 ft]; sweep_H=242 mm; sweep_H1=26 mm; sweep_box1=24 mm  [stored 0.0787402 ft]; sweep_box2=11 mm  [stored 0.0360892 ft]; w1=202 mm; w2=202 mm
- DN200_PN10 Flow range ( 190 - 339): Actuator_L=91 mm; Actuator_L1=82 mm; Actuator_d=47 mm; Body_H=204 mm; Body_Rib_L=85 mm; Bolt_Dia=23 mm; Bonnet_D=102 mm; Bonnet_D1=204 mm; Bonnet_R=214 mm; Bonnet_dim1=143 mm; Bonnet_dim1_H=19 mm  [stored 0.062336 ft]; Bonnet_dim1_H1=266 mm; Bonnet_dim2=71 mm; Bonnet_dim3=54 mm; Bore=100 mm; Bore1=120 mm; Bore2=160 mm; Centre_D=60 mm; Centre_D1=48 mm; Centre_nut=45 mm  [stored 0.147638 ft]; Control_dim1=13 mm  [stored 0.0426509 ft]; Control_dim2=64 mm; Control_dim3=7 mm  [stored 0.0229659 ft]; Control_dim4=184 mm; Control_dim5=18 mm  [stored 0.0590551 ft]; Control_dim6=22 mm  [stored 0.0721785 ft]; Control_dim7=39 mm; D=170 mm; DN=200 mm; FL_T=20 mm  [stored 0.0656168 ft]; H3=542 mm; H33=85 mm; H4=170 mm; L=600 mm; L3=236 mm; Nut_Dim1=30 mm  [stored 0.0984252 ft]; Nut_Dim2=5 mm  [stored 0.0164042 ft]; Nut_T=16 mm  [stored 0.0524934 ft]; Orifice_FL=136 mm; Raised_R=28 mm  [stored 0.0918635 ft]; Raised_dis=3 mm  [stored 0.00984252 ft]; Sweep_R=13 mm  [stored 0.0426509 ft]; Thickness=12 mm  [stored 0.0393701 ft]; Thickness1=14 mm  [stored 0.0459318 ft]; Total_L=615 mm; W=193 mm; W1=202 mm; W11=166 mm; W2=202 mm; W22=162 mm; centre=156 mm; dim1=81 mm; nut_dim=102 mm; sweep=21 mm  [stored 0.0688976 ft]; sweep/2=4 mm  [stored 0.0131234 ft]; sweep1=9 mm  [stored 0.0295276 ft]; sweep_D=18 mm  [stored 0.0590551 ft]; sweep_H=242 mm; sweep_H1=26 mm; sweep_box1=24 mm  [stored 0.0787402 ft]; sweep_box2=11 mm  [stored 0.0360892 ft]; w1=202 mm; w2=202 mm
- DN200_PN16 Flow range ( 50 - 130): Actuator_L=91 mm; Actuator_L1=82 mm; Actuator_d=47 mm; Body_H=204 mm; Body_Rib_L=85 mm; Bolt_Dia=23 mm; Bonnet_D=102 mm; Bonnet_D1=204 mm; Bonnet_R=214 mm; Bonnet_dim1=143 mm; Bonnet_dim1_H=19 mm  [stored 0.062336 ft]; Bonnet_dim1_H1=266 mm; Bonnet_dim2=71 mm; Bonnet_dim3=54 mm; Bore=100 mm; Bore1=120 mm; Bore2=161 mm; Centre_D=60 mm; Centre_D1=48 mm; Centre_nut=45 mm  [stored 0.147638 ft]; Control_dim1=13 mm  [stored 0.0426509 ft]; Control_dim2=64 mm; Control_dim3=7 mm  [stored 0.0229659 ft]; Control_dim4=184 mm; Control_dim5=18 mm  [stored 0.0590551 ft]; Control_dim6=22 mm  [stored 0.0721785 ft]; Control_dim7=39 mm; D=170 mm; DN=201 mm; FL_T=20 mm  [stored 0.0656168 ft]; H3=542 mm; H33=85 mm; H4=170 mm; L=600 mm; L3=236 mm; Nut_Dim1=30 mm  [stored 0.0984252 ft]; Nut_Dim2=5 mm  [stored 0.0164042 ft]; Nut_T=16 mm  [stored 0.0524934 ft]; Orifice_FL=136 mm; Raised_R=28 mm  [stored 0.0918635 ft]; Raised_dis=3 mm  [stored 0.00984252 ft]; Sweep_R=13 mm  [stored 0.0426509 ft]; Thickness=12 mm  [stored 0.0393701 ft]; Thickness1=14 mm  [stored 0.0459318 ft]; Total_L=615 mm; W=193 mm; W1=202 mm; W11=166 mm; W2=202 mm; W22=162 mm; centre=157 mm; dim1=81 mm; nut_dim=102 mm; sweep=21 mm  [stored 0.0688976 ft]; sweep/2=4 mm  [stored 0.0131234 ft]; sweep1=9 mm  [stored 0.0295276 ft]; sweep_D=18 mm  [stored 0.0590551 ft]; sweep_H=242 mm; sweep_H1=26 mm; sweep_box1=24 mm  [stored 0.0787402 ft]; sweep_box2=11 mm  [stored 0.0360892 ft]; w1=202 mm; w2=202 mm
- DN200_PN16 Flow range ( 115 - 290): Actuator_L=91 mm; Actuator_L1=82 mm; Actuator_d=47 mm; Body_H=204 mm; Body_Rib_L=85 mm; Bolt_Dia=23 mm; Bonnet_D=102 mm; Bonnet_D1=204 mm; Bonnet_R=214 mm; Bonnet_dim1=143 mm; Bonnet_dim1_H=19 mm  [stored 0.062336 ft]; Bonnet_dim1_H1=266 mm; Bonnet_dim2=71 mm; Bonnet_dim3=54 mm; Bore=100 mm; Bore1=120 mm; Bore2=160 mm; Centre_D=60 mm; Centre_D1=48 mm; Centre_nut=45 mm  [stored 0.147638 ft]; Control_dim1=13 mm  [stored 0.0426509 ft]; Control_dim2=64 mm; Control_dim3=7 mm  [stored 0.0229659 ft]; Control_dim4=184 mm; Control_dim5=18 mm  [stored 0.0590551 ft]; Control_dim6=22 mm  [stored 0.0721785 ft]; Control_dim7=39 mm; D=170 mm; DN=201 mm; FL_T=20 mm  [stored 0.0656168 ft]; H3=542 mm; H33=85 mm; H4=170 mm; L=600 mm; L3=236 mm; Nut_Dim1=30 mm  [stored 0.0984252 ft]; Nut_Dim2=5 mm  [stored 0.0164042 ft]; Nut_T=16 mm  [stored 0.0524934 ft]; Orifice_FL=136 mm; Raised_R=28 mm  [stored 0.0918635 ft]; Raised_dis=3 mm  [stored 0.00984252 ft]; Sweep_R=13 mm  [stored 0.0426509 ft]; Thickness=12 mm  [stored 0.0393701 ft]; Thickness1=14 mm  [stored 0.0459318 ft]; Total_L=615 mm; W=193 mm; W1=202 mm; W11=166 mm; W2=202 mm; W22=162 mm; centre=156 mm; dim1=81 mm; nut_dim=102 mm; sweep=21 mm  [stored 0.0688976 ft]; sweep/2=4 mm  [stored 0.0131234 ft]; sweep1=9 mm  [stored 0.0295276 ft]; sweep_D=18 mm  [stored 0.0590551 ft]; sweep_H=242 mm; sweep_H1=26 mm; sweep_box1=24 mm  [stored 0.0787402 ft]; sweep_box2=11 mm  [stored 0.0360892 ft]; w1=202 mm; w2=202 mm
- DN200_PN16 Flow range ( 150 - 365): Actuator_L=91 mm; Actuator_L1=82 mm; Actuator_d=47 mm; Body_H=204 mm; Body_Rib_L=85 mm; Bolt_Dia=23 mm; Bonnet_D=102 mm; Bonnet_D1=204 mm; Bonnet_R=214 mm; Bonnet_dim1=143 mm; Bonnet_dim1_H=19 mm  [stored 0.062336 ft]; Bonnet_dim1_H1=266 mm; Bonnet_dim2=71 mm; Bonnet_dim3=54 mm; Bore=100 mm; Bore1=120 mm; Bore2=160 mm; Centre_D=60 mm; Centre_D1=48 mm; Centre_nut=45 mm  [stored 0.147638 ft]; Control_dim1=13 mm  [stored 0.0426509 ft]; Control_dim2=64 mm; Control_dim3=7 mm  [stored 0.0229659 ft]; Control_dim4=184 mm; Control_dim5=18 mm  [stored 0.0590551 ft]; Control_dim6=22 mm  [stored 0.0721785 ft]; Control_dim7=39 mm; D=170 mm; DN=201 mm; FL_T=20 mm  [stored 0.0656168 ft]; H3=542 mm; H33=85 mm; H4=170 mm; L=600 mm; L3=236 mm; Nut_Dim1=30 mm  [stored 0.0984252 ft]; Nut_Dim2=5 mm  [stored 0.0164042 ft]; Nut_T=16 mm  [stored 0.0524934 ft]; Orifice_FL=136 mm; Raised_R=28 mm  [stored 0.0918635 ft]; Raised_dis=3 mm  [stored 0.00984252 ft]; Sweep_R=13 mm  [stored 0.0426509 ft]; Thickness=12 mm  [stored 0.0393701 ft]; Thickness1=14 mm  [stored 0.0459318 ft]; Total_L=615 mm; W=193 mm; W1=202 mm; W11=166 mm; W2=202 mm; W22=162 mm; centre=156 mm; dim1=81 mm; nut_dim=102 mm; sweep=21 mm  [stored 0.0688976 ft]; sweep/2=4 mm  [stored 0.0131234 ft]; sweep1=9 mm  [stored 0.0295276 ft]; sweep_D=18 mm  [stored 0.0590551 ft]; sweep_H=242 mm; sweep_H1=26 mm; sweep_box1=24 mm  [stored 0.0787402 ft]; sweep_box2=11 mm  [stored 0.0360892 ft]; w1=202 mm; w2=202 mm
- DN200_PN16 Flow range ( 190 - 452): Actuator_L=91 mm; Actuator_L1=82 mm; Actuator_d=47 mm; Body_H=204 mm; Body_Rib_L=85 mm; Bolt_Dia=23 mm; Bonnet_D=102 mm; Bonnet_D1=204 mm; Bonnet_R=214 mm; Bonnet_dim1=143 mm; Bonnet_dim1_H=19 mm  [stored 0.062336 ft]; Bonnet_dim1_H1=266 mm; Bonnet_dim2=71 mm; Bonnet_dim3=54 mm; Bore=100 mm; Bore1=120 mm; Bore2=161 mm; Centre_D=60 mm; Centre_D1=48 mm; Centre_nut=45 mm  [stored 0.147638 ft]; Control_dim1=13 mm  [stored 0.0426509 ft]; Control_dim2=64 mm; Control_dim3=7 mm  [stored 0.0229659 ft]; Control_dim4=184 mm; Control_dim5=18 mm  [stored 0.0590551 ft]; Control_dim6=22 mm  [stored 0.0721785 ft]; Control_dim7=39 mm; D=170 mm; DN=201 mm; FL_T=20 mm  [stored 0.0656168 ft]; H3=542 mm; H33=85 mm; H4=170 mm; L=600 mm; L3=236 mm; Nut_Dim1=30 mm  [stored 0.0984252 ft]; Nut_Dim2=5 mm  [stored 0.0164042 ft]; Nut_T=16 mm  [stored 0.0524934 ft]; Orifice_FL=136 mm; Raised_R=28 mm  [stored 0.0918635 ft]; Raised_dis=3 mm  [stored 0.00984252 ft]; Sweep_R=13 mm  [stored 0.0426509 ft]; Thickness=12 mm  [stored 0.0393701 ft]; Thickness1=14 mm  [stored 0.0459318 ft]; Total_L=615 mm; W=193 mm; W1=202 mm; W11=166 mm; W2=202 mm; W22=162 mm; centre=157 mm; dim1=81 mm; nut_dim=102 mm; sweep=21 mm  [stored 0.0688976 ft]; sweep/2=4 mm  [stored 0.0131234 ft]; sweep1=9 mm  [stored 0.0295276 ft]; sweep_D=18 mm  [stored 0.0590551 ft]; sweep_H=242 mm; sweep_H1=26 mm; sweep_box1=24 mm  [stored 0.0787402 ft]; sweep_box2=11 mm  [stored 0.0360892 ft]; w1=202 mm; w2=202 mm
- DN250_PN10 Flow range ( 85 - 200): Actuator_L=113 mm; Actuator_L1=102 mm; Actuator_d=56 mm; Body_H=243 mm; Body_Rib_L=101 mm; Bolt_Dia=26 mm; Bonnet_D=122 mm; Bonnet_D1=243 mm; Bonnet_R=255 mm; Bonnet_dim1=170 mm; Bonnet_dim1_H=27 mm; Bonnet_dim1_H1=326 mm; Bonnet_dim2=85 mm; Bonnet_dim3=64 mm; Bore=125 mm; Bore1=150 mm; Bore2=200 mm; Centre_D=70 mm; Centre_D1=56 mm; Centre_nut=53 mm; Control_dim1=16 mm  [stored 0.0524934 ft]; Control_dim2=77 mm; Control_dim3=8 mm  [stored 0.0262467 ft]; Control_dim4=219 mm; Control_dim5=22 mm  [stored 0.0721785 ft]; Control_dim6=26 mm; Control_dim7=47 mm; D=203 mm; DN=250 mm; FL_T=22 mm  [stored 0.0721785 ft]; H3=659 mm; H33=104 mm; H4=208 mm; L=730 mm; L3=281 mm; Nut_Dim1=34 mm; Nut_Dim2=6 mm  [stored 0.019685 ft]; Nut_T=18 mm  [stored 0.0590551 ft]; Orifice_FL=164 mm; Raised_R=31 mm; Raised_dis=3 mm  [stored 0.00984252 ft]; Sweep_R=15 mm  [stored 0.0492126 ft]; Thickness=13 mm  [stored 0.0426509 ft]; Thickness1=16 mm  [stored 0.0524934 ft]; Total_L=745 mm; W=242 mm; W1=252 mm; W11=209 mm; W2=252 mm; W22=202 mm; centre=195 mm; dim1=101 mm; nut_dim=122 mm; sweep=24 mm  [stored 0.0787402 ft]; sweep/2=5 mm  [stored 0.0164042 ft]; sweep1=10 mm  [stored 0.0328084 ft]; sweep_D=20 mm  [stored 0.0656168 ft]; sweep_H=297 mm; sweep_H1=38 mm; sweep_box1=28 mm  [stored 0.0918635 ft]; sweep_box2=13 mm  [stored 0.0426509 ft]; w1=252 mm; w2=252 mm
- DN250_PN10 Flow range ( 140 - 350): Actuator_L=113 mm; Actuator_L1=102 mm; Actuator_d=56 mm; Body_H=243 mm; Body_Rib_L=101 mm; Bolt_Dia=26 mm; Bonnet_D=122 mm; Bonnet_D1=243 mm; Bonnet_R=255 mm; Bonnet_dim1=170 mm; Bonnet_dim1_H=27 mm; Bonnet_dim1_H1=326 mm; Bonnet_dim2=85 mm; Bonnet_dim3=64 mm; Bore=125 mm; Bore1=150 mm; Bore2=200 mm; Centre_D=70 mm; Centre_D1=56 mm; Centre_nut=53 mm; Control_dim1=16 mm  [stored 0.0524934 ft]; Control_dim2=77 mm; Control_dim3=8 mm  [stored 0.0262467 ft]; Control_dim4=219 mm; Control_dim5=22 mm  [stored 0.0721785 ft]; Control_dim6=26 mm; Control_dim7=47 mm; D=203 mm; DN=250 mm; FL_T=22 mm  [stored 0.0721785 ft]; H3=659 mm; H33=104 mm; H4=208 mm; L=730 mm; L3=281 mm; Nut_Dim1=34 mm; Nut_Dim2=6 mm  [stored 0.019685 ft]; Nut_T=18 mm  [stored 0.0590551 ft]; Orifice_FL=164 mm; Raised_R=31 mm; Raised_dis=3 mm  [stored 0.00984252 ft]; Sweep_R=15 mm  [stored 0.0492126 ft]; Thickness=13 mm  [stored 0.0426509 ft]; Thickness1=16 mm  [stored 0.0524934 ft]; Total_L=745 mm; W=242 mm; W1=252 mm; W11=209 mm; W2=252 mm; W22=202 mm; centre=195 mm; dim1=101 mm; nut_dim=122 mm; sweep=24 mm  [stored 0.0787402 ft]; sweep/2=5 mm  [stored 0.0164042 ft]; sweep1=10 mm  [stored 0.0328084 ft]; sweep_D=20 mm  [stored 0.0656168 ft]; sweep_H=297 mm; sweep_H1=38 mm; sweep_box1=28 mm  [stored 0.0918635 ft]; sweep_box2=13 mm  [stored 0.0426509 ft]; w1=252 mm; w2=252 mm
- DN250_PN10 Flow range ( 230 - 530): Actuator_L=113 mm; Actuator_L1=102 mm; Actuator_d=56 mm; Body_H=243 mm; Body_Rib_L=101 mm; Bolt_Dia=26 mm; Bonnet_D=122 mm; Bonnet_D1=243 mm; Bonnet_R=255 mm; Bonnet_dim1=170 mm; Bonnet_dim1_H=27 mm; Bonnet_dim1_H1=326 mm; Bonnet_dim2=85 mm; Bonnet_dim3=64 mm; Bore=125 mm; Bore1=150 mm; Bore2=200 mm; Centre_D=70 mm; Centre_D1=56 mm; Centre_nut=53 mm; Control_dim1=16 mm  [stored 0.0524934 ft]; Control_dim2=77 mm; Control_dim3=8 mm  [stored 0.0262467 ft]; Control_dim4=219 mm; Control_dim5=22 mm  [stored 0.0721785 ft]; Control_dim6=26 mm; Control_dim7=47 mm; D=203 mm; DN=250 mm; FL_T=22 mm  [stored 0.0721785 ft]; H3=659 mm; H33=104 mm; H4=208 mm; L=730 mm; L3=281 mm; Nut_Dim1=34 mm; Nut_Dim2=6 mm  [stored 0.019685 ft]; Nut_T=18 mm  [stored 0.0590551 ft]; Orifice_FL=164 mm; Raised_R=31 mm; Raised_dis=3 mm  [stored 0.00984252 ft]; Sweep_R=15 mm  [stored 0.0492126 ft]; Thickness=13 mm  [stored 0.0426509 ft]; Thickness1=16 mm  [stored 0.0524934 ft]; Total_L=745 mm; W=242 mm; W1=252 mm; W11=209 mm; W2=252 mm; W22=202 mm; centre=195 mm; dim1=101 mm; nut_dim=122 mm; sweep=24 mm  [stored 0.0787402 ft]; sweep/2=5 mm  [stored 0.0164042 ft]; sweep1=10 mm  [stored 0.0328084 ft]; sweep_D=20 mm  [stored 0.0656168 ft]; sweep_H=297 mm; sweep_H1=38 mm; sweep_box1=28 mm  [stored 0.0918635 ft]; sweep_box2=13 mm  [stored 0.0426509 ft]; w1=252 mm; w2=252 mm
- DN250_PN10 Flow range ( 280 - 530): Actuator_L=113 mm; Actuator_L1=102 mm; Actuator_d=56 mm; Body_H=243 mm; Body_Rib_L=101 mm; Bolt_Dia=26 mm; Bonnet_D=122 mm; Bonnet_D1=243 mm; Bonnet_R=255 mm; Bonnet_dim1=170 mm; Bonnet_dim1_H=27 mm; Bonnet_dim1_H1=326 mm; Bonnet_dim2=85 mm; Bonnet_dim3=64 mm; Bore=125 mm; Bore1=150 mm; Bore2=200 mm; Centre_D=70 mm; Centre_D1=56 mm; Centre_nut=53 mm; Control_dim1=16 mm  [stored 0.0524934 ft]; Control_dim2=77 mm; Control_dim3=8 mm  [stored 0.0262467 ft]; Control_dim4=219 mm; Control_dim5=22 mm  [stored 0.0721785 ft]; Control_dim6=26 mm; Control_dim7=47 mm; D=203 mm; DN=250 mm; FL_T=22 mm  [stored 0.0721785 ft]; H3=659 mm; H33=104 mm; H4=208 mm; L=730 mm; L3=281 mm; Nut_Dim1=34 mm; Nut_Dim2=6 mm  [stored 0.019685 ft]; Nut_T=18 mm  [stored 0.0590551 ft]; Orifice_FL=164 mm; Raised_R=31 mm; Raised_dis=3 mm  [stored 0.00984252 ft]; Sweep_R=15 mm  [stored 0.0492126 ft]; Thickness=13 mm  [stored 0.0426509 ft]; Thickness1=16 mm  [stored 0.0524934 ft]; Total_L=745 mm; W=242 mm; W1=252 mm; W11=209 mm; W2=252 mm; W22=202 mm; centre=195 mm; dim1=101 mm; nut_dim=122 mm; sweep=24 mm  [stored 0.0787402 ft]; sweep/2=5 mm  [stored 0.0164042 ft]; sweep1=10 mm  [stored 0.0328084 ft]; sweep_D=20 mm  [stored 0.0656168 ft]; sweep_H=297 mm; sweep_H1=38 mm; sweep_box1=28 mm  [stored 0.0918635 ft]; sweep_box2=13 mm  [stored 0.0426509 ft]; w1=252 mm; w2=252 mm
- DN250_PN16 Flow range ( 85 - 200): Actuator_L=113 mm; Actuator_L1=102 mm; Actuator_d=56 mm; Body_H=243 mm; Body_Rib_L=101 mm; Bolt_Dia=26 mm; Bonnet_D=122 mm; Bonnet_D1=243 mm; Bonnet_R=255 mm; Bonnet_dim1=170 mm; Bonnet_dim1_H=27 mm; Bonnet_dim1_H1=326 mm; Bonnet_dim2=85 mm; Bonnet_dim3=64 mm; Bore=125 mm; Bore1=150 mm; Bore2=200 mm; Centre_D=70 mm; Centre_D1=56 mm; Centre_nut=53 mm; Control_dim1=16 mm  [stored 0.0524934 ft]; Control_dim2=77 mm; Control_dim3=8 mm  [stored 0.0262467 ft]; Control_dim4=219 mm; Control_dim5=22 mm  [stored 0.0721785 ft]; Control_dim6=26 mm; Control_dim7=47 mm; D=203 mm; DN=250 mm; FL_T=22 mm  [stored 0.0721785 ft]; H3=659 mm; H33=104 mm; H4=208 mm; L=730 mm; L3=281 mm; Nut_Dim1=34 mm; Nut_Dim2=6 mm  [stored 0.019685 ft]; Nut_T=18 mm  [stored 0.0590551 ft]; Orifice_FL=164 mm; Raised_R=31 mm; Raised_dis=3 mm  [stored 0.00984252 ft]; Sweep_R=15 mm  [stored 0.0492126 ft]; Thickness=13 mm  [stored 0.0426509 ft]; Thickness1=16 mm  [stored 0.0524934 ft]; Total_L=745 mm; W=242 mm; W1=252 mm; W11=209 mm; W2=252 mm; W22=202 mm; centre=195 mm; dim1=101 mm; nut_dim=122 mm; sweep=24 mm  [stored 0.0787402 ft]; sweep/2=5 mm  [stored 0.0164042 ft]; sweep1=10 mm  [stored 0.0328084 ft]; sweep_D=20 mm  [stored 0.0656168 ft]; sweep_H=297 mm; sweep_H1=38 mm; sweep_box1=28 mm  [stored 0.0918635 ft]; sweep_box2=13 mm  [stored 0.0426509 ft]; w1=252 mm; w2=252 mm
- DN250_PN16 Flow range ( 140 - 350): Actuator_L=113 mm; Actuator_L1=102 mm; Actuator_d=56 mm; Body_H=243 mm; Body_Rib_L=101 mm; Bolt_Dia=26 mm; Bonnet_D=122 mm; Bonnet_D1=243 mm; Bonnet_R=255 mm; Bonnet_dim1=170 mm; Bonnet_dim1_H=27 mm; Bonnet_dim1_H1=326 mm; Bonnet_dim2=85 mm; Bonnet_dim3=64 mm; Bore=125 mm; Bore1=150 mm; Bore2=200 mm; Centre_D=70 mm; Centre_D1=56 mm; Centre_nut=53 mm; Control_dim1=16 mm  [stored 0.0524934 ft]; Control_dim2=77 mm; Control_dim3=8 mm  [stored 0.0262467 ft]; Control_dim4=219 mm; Control_dim5=22 mm  [stored 0.0721785 ft]; Control_dim6=26 mm; Control_dim7=47 mm; D=203 mm; DN=250 mm; FL_T=22 mm  [stored 0.0721785 ft]; H3=659 mm; H33=104 mm; H4=208 mm; L=730 mm; L3=281 mm; Nut_Dim1=34 mm; Nut_Dim2=6 mm  [stored 0.019685 ft]; Nut_T=18 mm  [stored 0.0590551 ft]; Orifice_FL=164 mm; Raised_R=31 mm; Raised_dis=3 mm  [stored 0.00984252 ft]; Sweep_R=15 mm  [stored 0.0492126 ft]; Thickness=13 mm  [stored 0.0426509 ft]; Thickness1=16 mm  [stored 0.0524934 ft]; Total_L=745 mm; W=242 mm; W1=252 mm; W11=209 mm; W2=252 mm; W22=202 mm; centre=195 mm; dim1=101 mm; nut_dim=122 mm; sweep=24 mm  [stored 0.0787402 ft]; sweep/2=5 mm  [stored 0.0164042 ft]; sweep1=10 mm  [stored 0.0328084 ft]; sweep_D=20 mm  [stored 0.0656168 ft]; sweep_H=297 mm; sweep_H1=38 mm; sweep_box1=28 mm  [stored 0.0918635 ft]; sweep_box2=13 mm  [stored 0.0426509 ft]; w1=252 mm; w2=252 mm
- DN250_PN16 Flow range ( 230 - 570): Actuator_L=113 mm; Actuator_L1=102 mm; Actuator_d=56 mm; Body_H=243 mm; Body_Rib_L=101 mm; Bolt_Dia=26 mm; Bonnet_D=122 mm; Bonnet_D1=243 mm; Bonnet_R=255 mm; Bonnet_dim1=170 mm; Bonnet_dim1_H=27 mm; Bonnet_dim1_H1=326 mm; Bonnet_dim2=85 mm; Bonnet_dim3=64 mm; Bore=125 mm; Bore1=150 mm; Bore2=200 mm; Centre_D=70 mm; Centre_D1=56 mm; Centre_nut=53 mm; Control_dim1=16 mm  [stored 0.0524934 ft]; Control_dim2=77 mm; Control_dim3=8 mm  [stored 0.0262467 ft]; Control_dim4=219 mm; Control_dim5=22 mm  [stored 0.0721785 ft]; Control_dim6=26 mm; Control_dim7=47 mm; D=203 mm; DN=250 mm; FL_T=22 mm  [stored 0.0721785 ft]; H3=659 mm; H33=104 mm; H4=208 mm; L=730 mm; L3=281 mm; Nut_Dim1=34 mm; Nut_Dim2=6 mm  [stored 0.019685 ft]; Nut_T=18 mm  [stored 0.0590551 ft]; Orifice_FL=164 mm; Raised_R=31 mm; Raised_dis=3 mm  [stored 0.00984252 ft]; Sweep_R=15 mm  [stored 0.0492126 ft]; Thickness=13 mm  [stored 0.0426509 ft]; Thickness1=16 mm  [stored 0.0524934 ft]; Total_L=745 mm; W=242 mm; W1=252 mm; W11=209 mm; W2=252 mm; W22=202 mm; centre=195 mm; dim1=101 mm; nut_dim=122 mm; sweep=24 mm  [stored 0.0787402 ft]; sweep/2=5 mm  [stored 0.0164042 ft]; sweep1=10 mm  [stored 0.0328084 ft]; sweep_D=20 mm  [stored 0.0656168 ft]; sweep_H=297 mm; sweep_H1=38 mm; sweep_box1=28 mm  [stored 0.0918635 ft]; sweep_box2=13 mm  [stored 0.0426509 ft]; w1=252 mm; w2=252 mm
- DN250_PN16 Flow range ( 280 - 690): Actuator_L=113 mm; Actuator_L1=102 mm; Actuator_d=56 mm; Body_H=243 mm; Body_Rib_L=101 mm; Bolt_Dia=26 mm; Bonnet_D=122 mm; Bonnet_D1=243 mm; Bonnet_R=255 mm; Bonnet_dim1=170 mm; Bonnet_dim1_H=27 mm; Bonnet_dim1_H1=326 mm; Bonnet_dim2=85 mm; Bonnet_dim3=64 mm; Bore=125 mm; Bore1=150 mm; Bore2=200 mm; Centre_D=70 mm; Centre_D1=56 mm; Centre_nut=53 mm; Control_dim1=16 mm  [stored 0.0524934 ft]; Control_dim2=77 mm; Control_dim3=8 mm  [stored 0.0262467 ft]; Control_dim4=219 mm; Control_dim5=22 mm  [stored 0.0721785 ft]; Control_dim6=26 mm; Control_dim7=47 mm; D=203 mm; DN=250 mm; FL_T=22 mm  [stored 0.0721785 ft]; H3=659 mm; H33=104 mm; H4=208 mm; L=730 mm; L3=281 mm; Nut_Dim1=34 mm; Nut_Dim2=6 mm  [stored 0.019685 ft]; Nut_T=18 mm  [stored 0.0590551 ft]; Orifice_FL=164 mm; Raised_R=31 mm; Raised_dis=3 mm  [stored 0.00984252 ft]; Sweep_R=15 mm  [stored 0.0492126 ft]; Thickness=13 mm  [stored 0.0426509 ft]; Thickness1=16 mm  [stored 0.0524934 ft]; Total_L=745 mm; W=242 mm; W1=252 mm; W11=209 mm; W2=252 mm; W22=202 mm; centre=195 mm; dim1=101 mm; nut_dim=122 mm; sweep=24 mm  [stored 0.0787402 ft]; sweep/2=5 mm  [stored 0.0164042 ft]; sweep1=10 mm  [stored 0.0328084 ft]; sweep_D=20 mm  [stored 0.0656168 ft]; sweep_H=297 mm; sweep_H1=38 mm; sweep_box1=28 mm  [stored 0.0918635 ft]; sweep_box2=13 mm  [stored 0.0426509 ft]; w1=252 mm; w2=252 mm
- DN300_PN10 Flow range ( 120 - 300): Actuator_L=124 mm; Actuator_L1=111 mm; Actuator_d=63 mm; Body_H=276 mm; Body_Rib_L=115 mm; Bolt_Dia=33 mm; Bonnet_D=138 mm; Bonnet_D1=276 mm; Bonnet_R=290 mm; Bonnet_dim1=193 mm; Bonnet_dim1_H=26 mm; Bonnet_dim1_H1=362 mm; Bonnet_dim2=97 mm; Bonnet_dim3=72 mm; Bore=150 mm; Bore1=180 mm; Bore2=240 mm; Centre_D=80 mm; Centre_D1=64 mm; Centre_nut=60 mm; Control_dim1=18 mm  [stored 0.0590551 ft]; Control_dim2=87 mm; Control_dim3=9 mm  [stored 0.0295276 ft]; Control_dim4=248 mm; Control_dim5=24 mm  [stored 0.0787402 ft]; Control_dim6=29 mm  [stored 0.0951444 ft]; Control_dim7=53 mm; D=230 mm; DN=300 mm; FL_T=25 mm  [stored 0.082021 ft]; H3=736 mm; H33=115 mm; H4=231 mm; L=850 mm; L3=319 mm; Nut_Dim1=42 mm  [stored 0.137795 ft]; Nut_Dim2=7 mm  [stored 0.0229659 ft]; Nut_T=20 mm  [stored 0.0656168 ft]; Orifice_FL=189 mm; Raised_R=32 mm  [stored 0.104987 ft]; Raised_dis=4 mm  [stored 0.0131234 ft]; Sweep_R=19 mm  [stored 0.062336 ft]; Thickness=15 mm  [stored 0.0492126 ft]; Thickness1=18 mm  [stored 0.0590551 ft]; Total_L=865 mm; W=263 mm; W1=275 mm; W11=225 mm; W2=275 mm; W22=220 mm; centre=234 mm; dim1=110 mm; nut_dim=138 mm; sweep=30 mm  [stored 0.0984252 ft]; sweep/2=6 mm  [stored 0.019685 ft]; sweep1=13 mm  [stored 0.0426509 ft]; sweep_D=25 mm  [stored 0.082021 ft]; sweep_H=329 mm; sweep_H1=37 mm; sweep_box1=32 mm  [stored 0.104987 ft]; sweep_box2=16 mm  [stored 0.0524934 ft]; w1=275 mm; w2=275 mm
- DN300_PN10 Flow range ( 175 - 430): Actuator_L=124 mm; Actuator_L1=111 mm; Actuator_d=63 mm; Body_H=276 mm; Body_Rib_L=115 mm; Bolt_Dia=33 mm; Bonnet_D=138 mm; Bonnet_D1=276 mm; Bonnet_R=290 mm; Bonnet_dim1=193 mm; Bonnet_dim1_H=26 mm; Bonnet_dim1_H1=362 mm; Bonnet_dim2=97 mm; Bonnet_dim3=72 mm; Bore=150 mm; Bore1=180 mm; Bore2=240 mm; Centre_D=80 mm; Centre_D1=64 mm; Centre_nut=60 mm; Control_dim1=18 mm  [stored 0.0590551 ft]; Control_dim2=87 mm; Control_dim3=9 mm  [stored 0.0295276 ft]; Control_dim4=248 mm; Control_dim5=24 mm  [stored 0.0787402 ft]; Control_dim6=29 mm  [stored 0.0951444 ft]; Control_dim7=53 mm; D=230 mm; DN=300 mm; FL_T=25 mm  [stored 0.082021 ft]; H3=736 mm; H33=115 mm; H4=231 mm; L=850 mm; L3=319 mm; Nut_Dim1=42 mm  [stored 0.137795 ft]; Nut_Dim2=7 mm  [stored 0.0229659 ft]; Nut_T=20 mm  [stored 0.0656168 ft]; Orifice_FL=189 mm; Raised_R=32 mm  [stored 0.104987 ft]; Raised_dis=4 mm  [stored 0.0131234 ft]; Sweep_R=19 mm  [stored 0.062336 ft]; Thickness=15 mm  [stored 0.0492126 ft]; Thickness1=18 mm  [stored 0.0590551 ft]; Total_L=865 mm; W=263 mm; W1=275 mm; W11=225 mm; W2=275 mm; W22=220 mm; centre=234 mm; dim1=110 mm; nut_dim=138 mm; sweep=30 mm  [stored 0.0984252 ft]; sweep/2=6 mm  [stored 0.019685 ft]; sweep1=13 mm  [stored 0.0426509 ft]; sweep_D=25 mm  [stored 0.082021 ft]; sweep_H=329 mm; sweep_H1=37 mm; sweep_box1=32 mm  [stored 0.104987 ft]; sweep_box2=16 mm  [stored 0.0524934 ft]; w1=275 mm; w2=275 mm
- DN300_PN10 Flow range ( 340 - 762): Actuator_L=124 mm; Actuator_L1=111 mm; Actuator_d=63 mm; Body_H=276 mm; Body_Rib_L=115 mm; Bolt_Dia=33 mm; Bonnet_D=138 mm; Bonnet_D1=276 mm; Bonnet_R=290 mm; Bonnet_dim1=193 mm; Bonnet_dim1_H=26 mm; Bonnet_dim1_H1=362 mm; Bonnet_dim2=97 mm; Bonnet_dim3=72 mm; Bore=150 mm; Bore1=180 mm; Bore2=240 mm; Centre_D=80 mm; Centre_D1=64 mm; Centre_nut=60 mm; Control_dim1=18 mm  [stored 0.0590551 ft]; Control_dim2=87 mm; Control_dim3=9 mm  [stored 0.0295276 ft]; Control_dim4=248 mm; Control_dim5=24 mm  [stored 0.0787402 ft]; Control_dim6=29 mm  [stored 0.0951444 ft]; Control_dim7=53 mm; D=230 mm; DN=300 mm; FL_T=25 mm  [stored 0.082021 ft]; H3=736 mm; H33=115 mm; H4=231 mm; L=850 mm; L3=319 mm; Nut_Dim1=42 mm  [stored 0.137795 ft]; Nut_Dim2=7 mm  [stored 0.0229659 ft]; Nut_T=20 mm  [stored 0.0656168 ft]; Orifice_FL=189 mm; Raised_R=32 mm  [stored 0.104987 ft]; Raised_dis=4 mm  [stored 0.0131234 ft]; Sweep_R=19 mm  [stored 0.062336 ft]; Thickness=15 mm  [stored 0.0492126 ft]; Thickness1=18 mm  [stored 0.0590551 ft]; Total_L=865 mm; W=263 mm; W1=275 mm; W11=225 mm; W2=275 mm; W22=220 mm; centre=234 mm; dim1=110 mm; nut_dim=138 mm; sweep=30 mm  [stored 0.0984252 ft]; sweep/2=6 mm  [stored 0.019685 ft]; sweep1=13 mm  [stored 0.0426509 ft]; sweep_D=25 mm  [stored 0.082021 ft]; sweep_H=329 mm; sweep_H1=37 mm; sweep_box1=32 mm  [stored 0.104987 ft]; sweep_box2=16 mm  [stored 0.0524934 ft]; w1=275 mm; w2=275 mm
- DN300_PN10 Flow range ( 460 - 762): Actuator_L=124 mm; Actuator_L1=111 mm; Actuator_d=63 mm; Body_H=276 mm; Body_Rib_L=115 mm; Bolt_Dia=33 mm; Bonnet_D=138 mm; Bonnet_D1=276 mm; Bonnet_R=290 mm; Bonnet_dim1=193 mm; Bonnet_dim1_H=26 mm; Bonnet_dim1_H1=362 mm; Bonnet_dim2=97 mm; Bonnet_dim3=72 mm; Bore=150 mm; Bore1=180 mm; Bore2=240 mm; Centre_D=80 mm; Centre_D1=64 mm; Centre_nut=60 mm; Control_dim1=18 mm  [stored 0.0590551 ft]; Control_dim2=87 mm; Control_dim3=9 mm  [stored 0.0295276 ft]; Control_dim4=248 mm; Control_dim5=24 mm  [stored 0.0787402 ft]; Control_dim6=29 mm  [stored 0.0951444 ft]; Control_dim7=53 mm; D=230 mm; DN=300 mm; FL_T=25 mm  [stored 0.082021 ft]; H3=736 mm; H33=115 mm; H4=231 mm; L=850 mm; L3=319 mm; Nut_Dim1=42 mm  [stored 0.137795 ft]; Nut_Dim2=7 mm  [stored 0.0229659 ft]; Nut_T=20 mm  [stored 0.0656168 ft]; Orifice_FL=189 mm; Raised_R=32 mm  [stored 0.104987 ft]; Raised_dis=4 mm  [stored 0.0131234 ft]; Sweep_R=19 mm  [stored 0.062336 ft]; Thickness=15 mm  [stored 0.0492126 ft]; Thickness1=18 mm  [stored 0.0590551 ft]; Total_L=865 mm; W=263 mm; W1=275 mm; W11=225 mm; W2=275 mm; W22=220 mm; centre=234 mm; dim1=110 mm; nut_dim=138 mm; sweep=30 mm  [stored 0.0984252 ft]; sweep/2=6 mm  [stored 0.019685 ft]; sweep1=13 mm  [stored 0.0426509 ft]; sweep_D=25 mm  [stored 0.082021 ft]; sweep_H=329 mm; sweep_H1=37 mm; sweep_box1=32 mm  [stored 0.104987 ft]; sweep_box2=16 mm  [stored 0.0524934 ft]; w1=275 mm; w2=275 mm
- DN300_PN16 Flow range ( 120 - 300): Actuator_L=124 mm; Actuator_L1=111 mm; Actuator_d=63 mm; Body_H=276 mm; Body_Rib_L=115 mm; Bolt_Dia=33 mm; Bonnet_D=138 mm; Bonnet_D1=276 mm; Bonnet_R=290 mm; Bonnet_dim1=193 mm; Bonnet_dim1_H=26 mm; Bonnet_dim1_H1=362 mm; Bonnet_dim2=97 mm; Bonnet_dim3=72 mm; Bore=150 mm; Bore1=180 mm; Bore2=240 mm; Centre_D=80 mm; Centre_D1=64 mm; Centre_nut=60 mm; Control_dim1=18 mm  [stored 0.0590551 ft]; Control_dim2=87 mm; Control_dim3=9 mm  [stored 0.0295276 ft]; Control_dim4=248 mm; Control_dim5=24 mm  [stored 0.0787402 ft]; Control_dim6=29 mm  [stored 0.0951444 ft]; Control_dim7=53 mm; D=230 mm; DN=300 mm; FL_T=25 mm  [stored 0.082021 ft]; H3=736 mm; H33=115 mm; H4=231 mm; L=850 mm; L3=319 mm; Nut_Dim1=42 mm  [stored 0.137795 ft]; Nut_Dim2=7 mm  [stored 0.0229659 ft]; Nut_T=20 mm  [stored 0.0656168 ft]; Orifice_FL=189 mm; Raised_R=32 mm  [stored 0.104987 ft]; Raised_dis=4 mm  [stored 0.0131234 ft]; Sweep_R=19 mm  [stored 0.062336 ft]; Thickness=15 mm  [stored 0.0492126 ft]; Thickness1=18 mm  [stored 0.0590551 ft]; Total_L=865 mm; W=263 mm; W1=275 mm; W11=225 mm; W2=275 mm; W22=220 mm; centre=234 mm; dim1=110 mm; nut_dim=138 mm; sweep=30 mm  [stored 0.0984252 ft]; sweep/2=6 mm  [stored 0.019685 ft]; sweep1=13 mm  [stored 0.0426509 ft]; sweep_D=25 mm  [stored 0.082021 ft]; sweep_H=329 mm; sweep_H1=37 mm; sweep_box1=32 mm  [stored 0.104987 ft]; sweep_box2=16 mm  [stored 0.0524934 ft]; w1=275 mm; w2=275 mm
- DN300_PN16 Flow range ( 175 - 430): Actuator_L=124 mm; Actuator_L1=111 mm; Actuator_d=63 mm; Body_H=276 mm; Body_Rib_L=115 mm; Bolt_Dia=33 mm; Bonnet_D=138 mm; Bonnet_D1=276 mm; Bonnet_R=290 mm; Bonnet_dim1=193 mm; Bonnet_dim1_H=26 mm; Bonnet_dim1_H1=362 mm; Bonnet_dim2=97 mm; Bonnet_dim3=72 mm; Bore=150 mm; Bore1=180 mm; Bore2=240 mm; Centre_D=80 mm; Centre_D1=64 mm; Centre_nut=60 mm; Control_dim1=18 mm  [stored 0.0590551 ft]; Control_dim2=87 mm; Control_dim3=9 mm  [stored 0.0295276 ft]; Control_dim4=248 mm; Control_dim5=24 mm  [stored 0.0787402 ft]; Control_dim6=29 mm  [stored 0.0951444 ft]; Control_dim7=53 mm; D=230 mm; DN=300 mm; FL_T=25 mm  [stored 0.082021 ft]; H3=736 mm; H33=115 mm; H4=231 mm; L=850 mm; L3=319 mm; Nut_Dim1=42 mm  [stored 0.137795 ft]; Nut_Dim2=7 mm  [stored 0.0229659 ft]; Nut_T=20 mm  [stored 0.0656168 ft]; Orifice_FL=189 mm; Raised_R=32 mm  [stored 0.104987 ft]; Raised_dis=4 mm  [stored 0.0131234 ft]; Sweep_R=19 mm  [stored 0.062336 ft]; Thickness=15 mm  [stored 0.0492126 ft]; Thickness1=18 mm  [stored 0.0590551 ft]; Total_L=865 mm; W=263 mm; W1=275 mm; W11=225 mm; W2=275 mm; W22=220 mm; centre=234 mm; dim1=110 mm; nut_dim=138 mm; sweep=30 mm  [stored 0.0984252 ft]; sweep/2=6 mm  [stored 0.019685 ft]; sweep1=13 mm  [stored 0.0426509 ft]; sweep_D=25 mm  [stored 0.082021 ft]; sweep_H=329 mm; sweep_H1=37 mm; sweep_box1=32 mm  [stored 0.104987 ft]; sweep_box2=16 mm  [stored 0.0524934 ft]; w1=275 mm; w2=275 mm
- DN300_PN16 Flow range ( 340 - 825): Actuator_L=124 mm; Actuator_L1=111 mm; Actuator_d=63 mm; Body_H=276 mm; Body_Rib_L=115 mm; Bolt_Dia=33 mm; Bonnet_D=138 mm; Bonnet_D1=276 mm; Bonnet_R=290 mm; Bonnet_dim1=193 mm; Bonnet_dim1_H=26 mm; Bonnet_dim1_H1=362 mm; Bonnet_dim2=97 mm; Bonnet_dim3=72 mm; Bore=150 mm; Bore1=180 mm; Bore2=240 mm; Centre_D=80 mm; Centre_D1=64 mm; Centre_nut=60 mm; Control_dim1=18 mm  [stored 0.0590551 ft]; Control_dim2=87 mm; Control_dim3=9 mm  [stored 0.0295276 ft]; Control_dim4=248 mm; Control_dim5=24 mm  [stored 0.0787402 ft]; Control_dim6=29 mm  [stored 0.0951444 ft]; Control_dim7=53 mm; D=230 mm; DN=300 mm; FL_T=25 mm  [stored 0.082021 ft]; H3=736 mm; H33=115 mm; H4=231 mm; L=850 mm; L3=319 mm; Nut_Dim1=42 mm  [stored 0.137795 ft]; Nut_Dim2=7 mm  [stored 0.0229659 ft]; Nut_T=20 mm  [stored 0.0656168 ft]; Orifice_FL=189 mm; Raised_R=32 mm  [stored 0.104987 ft]; Raised_dis=4 mm  [stored 0.0131234 ft]; Sweep_R=19 mm  [stored 0.062336 ft]; Thickness=15 mm  [stored 0.0492126 ft]; Thickness1=18 mm  [stored 0.0590551 ft]; Total_L=865 mm; W=263 mm; W1=275 mm; W11=225 mm; W2=275 mm; W22=220 mm; centre=234 mm; dim1=110 mm; nut_dim=138 mm; sweep=30 mm  [stored 0.0984252 ft]; sweep/2=6 mm  [stored 0.019685 ft]; sweep1=13 mm  [stored 0.0426509 ft]; sweep_D=25 mm  [stored 0.082021 ft]; sweep_H=329 mm; sweep_H1=37 mm; sweep_box1=32 mm  [stored 0.104987 ft]; sweep_box2=16 mm  [stored 0.0524934 ft]; w1=275 mm; w2=275 mm
- DN300_PN16 Flow range ( 460 - 1017): Actuator_L=124 mm; Actuator_L1=111 mm; Actuator_d=63 mm; Body_H=276 mm; Body_Rib_L=115 mm; Bolt_Dia=33 mm; Bonnet_D=138 mm; Bonnet_D1=276 mm; Bonnet_R=290 mm; Bonnet_dim1=193 mm; Bonnet_dim1_H=26 mm; Bonnet_dim1_H1=362 mm; Bonnet_dim2=97 mm; Bonnet_dim3=72 mm; Bore=150 mm; Bore1=180 mm; Bore2=240 mm; Centre_D=80 mm; Centre_D1=64 mm; Centre_nut=60 mm; Control_dim1=18 mm  [stored 0.0590551 ft]; Control_dim2=87 mm; Control_dim3=9 mm  [stored 0.0295276 ft]; Control_dim4=248 mm; Control_dim5=24 mm  [stored 0.0787402 ft]; Control_dim6=29 mm  [stored 0.0951444 ft]; Control_dim7=53 mm; D=230 mm; DN=300 mm; FL_T=25 mm  [stored 0.082021 ft]; H3=736 mm; H33=115 mm; H4=231 mm; L=850 mm; L3=319 mm; Nut_Dim1=42 mm  [stored 0.137795 ft]; Nut_Dim2=7 mm  [stored 0.0229659 ft]; Nut_T=20 mm  [stored 0.0656168 ft]; Orifice_FL=189 mm; Raised_R=32 mm  [stored 0.104987 ft]; Raised_dis=4 mm  [stored 0.0131234 ft]; Sweep_R=19 mm  [stored 0.062336 ft]; Thickness=15 mm  [stored 0.0492126 ft]; Thickness1=18 mm  [stored 0.0590551 ft]; Total_L=865 mm; W=263 mm; W1=275 mm; W11=225 mm; W2=275 mm; W22=220 mm; centre=234 mm; dim1=110 mm; nut_dim=138 mm; sweep=30 mm  [stored 0.0984252 ft]; sweep/2=6 mm  [stored 0.019685 ft]; sweep1=13 mm  [stored 0.0426509 ft]; sweep_D=25 mm  [stored 0.082021 ft]; sweep_H=329 mm; sweep_H1=37 mm; sweep_box1=32 mm  [stored 0.104987 ft]; sweep_box2=16 mm  [stored 0.0524934 ft]; w1=275 mm; w2=275 mm

note: [stored X ft] marks values corroborated as IEEE doubles in the binary element streams (Revit-internal decimal feet)

## geometry (parser evidence)
native form markers: Sweep x7
no freeform markers — native parametric forms only
